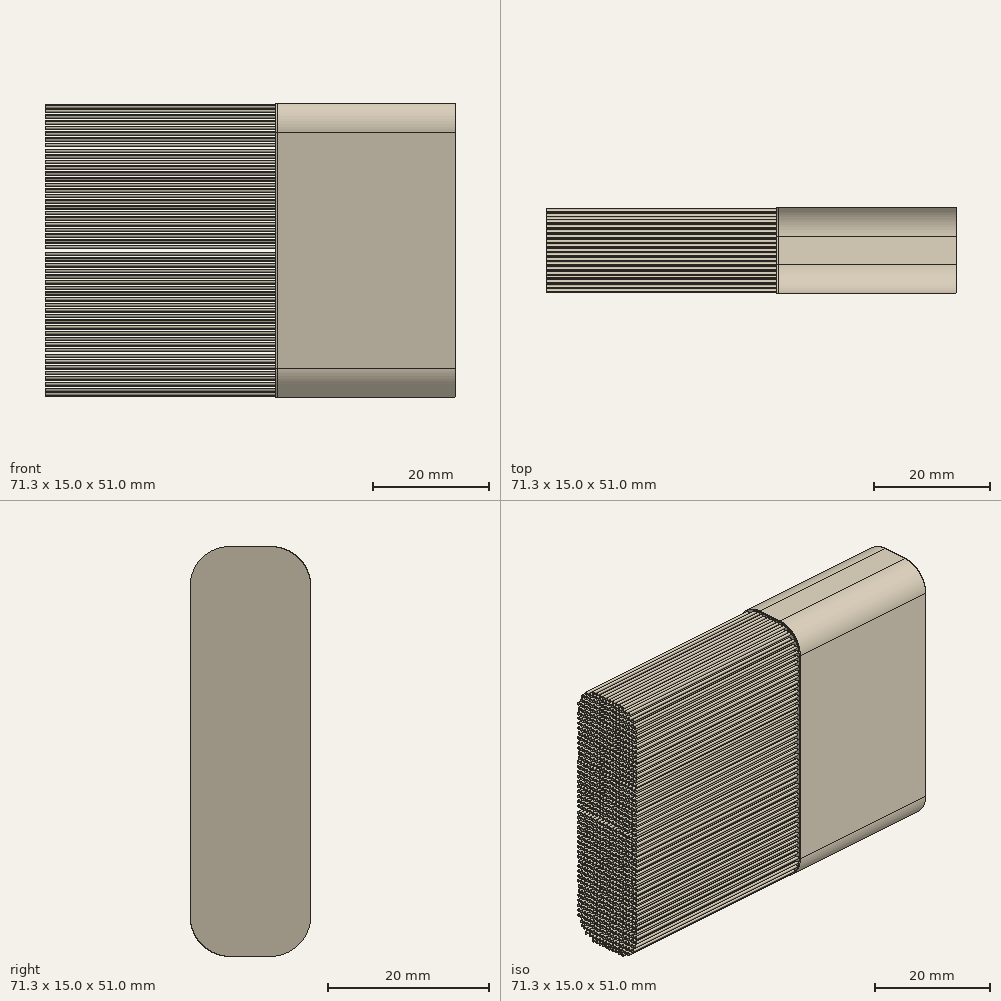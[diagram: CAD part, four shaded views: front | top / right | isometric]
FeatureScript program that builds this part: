
annotation { "Feature Type Name" : "Feature", "Feature Type Description" : "" }
export const myFeature = defineFeature(function(context is Context, id is Id, definition is map)
    precondition{}
    {
        {
            var Q0;
            Q0=qCreatedBy(makeId("Front.planeOp"),FACE);
            var sketch = newSketch(context, id + "F0", { "sketchPlane" : qUnion([Q0])});
            skLineSegment(sketch, "E0.bottom", {"start": v(15.5, -25.5) * mm, "end": v(-15.5, -25.5) * mm});
            skLineSegment(sketch, "E0.top", {"start": v(15.5, 25.5) * mm, "end": v(-15.5, 25.5) * mm});
            skLineSegment(sketch, "E0.left", {"start": v(15.5, -25.5) * mm, "end": v(15.5, 25.5) * mm});
            skLineSegment(sketch, "E0.right", {"start": v(-15.5, -25.5) * mm, "end": v(-15.5, 25.5) * mm});
            skPoint(sketch, "E0.middle", {"position": v(0, 0) * mm});
            skSolve(sketch);
        }
        {
            var Q0;
            Q0=makeQuery(id+"F0.imprint","IMPRINT",FACE,{"disambiguationData":[TD([[makeQuery(id+"F0.imprint","IMPRINT",EDGE,{"derivedFrom":sQuery(id+"F0.wireOp",EDGE,"E0.bottom")}),-1.0]])]});
            extrude(context, id + "F1", {"entities" : qUnion([Q0]), "depth" : 15 * mm});
        }
        {
            var Q0;
            Q0=makeQuery(id+"F1.opExtrude","CAP_EDGE",EDGE,{"disambiguationData":[OSD([sQuery(id+"F0.wireOp",EDGE,"E0.top")])],"isStart":true});
            var Q1;
            Q1=makeQuery(id+"F1.opExtrude","CAP_EDGE",EDGE,{"disambiguationData":[OSD([sQuery(id+"F0.wireOp",EDGE,"E0.bottom")])],"isStart":true});
            var Q2;
            Q2=makeQuery(id+"F1.opExtrude","CAP_EDGE",EDGE,{"disambiguationData":[OSD([sQuery(id+"F0.wireOp",EDGE,"E0.bottom")])],"isStart":false});
            var Q3;
            Q3=makeQuery(id+"F1.opExtrude","CAP_EDGE",EDGE,{"disambiguationData":[OSD([sQuery(id+"F0.wireOp",EDGE,"E0.top")])],"isStart":false});
            fillet(context, id + "F2", {"entities" : qUnion([Q0, Q1, Q2, Q3]), "radius" : 5 * mm, "tangentPropagation" : true, "allowEdgeOverflow" : false});
        }
        {
            var Q0;
            Q0=qCreatedBy(makeId("Right.planeOp"),FACE);
            cPlane(context, id + "F3", {"entities" : qUnion([Q0]), "cplaneType" : CPlaneType.OFFSET, "offset" : 15.8 * mm, "oppositeDirection" : true, "width" : 150 * mm, "height" : 150 * mm});
        }
        {
            var Q0;
            Q0=qCreatedBy(id+"F3.planeOp",FACE);
            var sketch = newSketch(context, id + "F4", { "sketchPlane" : qUnion([Q0])});
            skLineSegment(sketch, "E1.0.0", {"start": v(-10, 25.5) * mm, "end": v(-5, 25.5) * mm});
            skArc(sketch, "E1.0.1", {"start": v(-5, 25.5) * mm, "mid": v(-1.46, 24.04) * mm, "end": v(0, 20.5) * mm});
            skLineSegment(sketch, "E1.0.2", {"start": v(0, 20.5) * mm, "end": v(0, -20.5) * mm});
            skArc(sketch, "E1.0.3", {"start": v(0, -20.5) * mm, "mid": v(-1.46, -24.04) * mm, "end": v(-5, -25.5) * mm});
            skLineSegment(sketch, "E1.0.4", {"start": v(-5, -25.5) * mm, "end": v(-10, -25.5) * mm});
            skArc(sketch, "E1.0.5", {"start": v(-10, -25.5) * mm, "mid": v(-13.54, -24.04) * mm, "end": v(-15, -20.5) * mm});
            skLineSegment(sketch, "E1.0.6", {"start": v(-15, -20.5) * mm, "end": v(-15, 20.5) * mm});
            skArc(sketch, "E1.0.7", {"start": v(-15, 20.5) * mm, "mid": v(-13.54, 24.04) * mm, "end": v(-10, 25.5) * mm});
            skSolve(sketch);
        }
        {
            var Q0;
            Q0=makeQuery(id+"F4.imprint","IMPRINT",FACE,{"disambiguationData":[TD([[makeQuery(id+"F4.imprint","IMPRINT",EDGE,{"derivedFrom":sQuery(id+"F4.wireOp",EDGE,"E1.0.0")}),-1.0]])]});
            extrude(context, id + "F5", {"entities" : qUnion([Q0]), "depth" : 0.3 * mm});
        }
        {
            var Q0;
            Q0=makeQuery(id+"F4.imprint","IMPRINT",FACE,{"disambiguationData":[TD([[makeQuery(id+"F4.imprint","IMPRINT",EDGE,{"derivedFrom":sQuery(id+"F4.wireOp",EDGE,"E1.0.0")}),-1.0]])]});
            var sketch = newSketch(context, id + "F6", { "sketchPlane" : qUnion([Q0])});
            skCircle(sketch, "E2", {"center": v(-8.78, 4.59) * mm, "radius": 0.25 * mm});
            skCircle(sketch, "E3", {"center": v(-9.57, 4.53) * mm, "radius": 0.25 * mm});
            skCircle(sketch, "E4", {"center": v(-10.4, 4.5) * mm, "radius": 0.25 * mm});
            skCircle(sketch, "E5", {"center": v(-11.22, 4.53) * mm, "radius": 0.25 * mm});
            skCircle(sketch, "E6", {"center": v(-8, 4.59) * mm, "radius": 0.25 * mm});
            skCircle(sketch, "E7", {"center": v(-13.64, 4.5) * mm, "radius": 0.25 * mm});
            skCircle(sketch, "E8", {"center": v(-11.98, 4.56) * mm, "radius": 0.25 * mm});
            skCircle(sketch, "E9", {"center": v(-14.45, 4.53) * mm, "radius": 0.25 * mm});
            skCircle(sketch, "E10", {"center": v(-0.37, 4.62) * mm, "radius": 0.25 * mm});
            skCircle(sketch, "E11", {"center": v(-12.74, 4.5) * mm, "radius": 0.25 * mm});
            skCircle(sketch, "E12", {"center": v(-6.43, 4.55) * mm, "radius": 0.25 * mm});
            skCircle(sketch, "E13", {"center": v(-5.64, 4.6) * mm, "radius": 0.25 * mm});
            skCircle(sketch, "E14", {"center": v(-4.8, 4.63) * mm, "radius": 0.25 * mm});
            skCircle(sketch, "E15", {"center": v(-3.99, 4.6) * mm, "radius": 0.25 * mm});
            skCircle(sketch, "E16", {"center": v(-7.22, 4.55) * mm, "radius": 0.25 * mm});
            skCircle(sketch, "E17", {"center": v(-1.78, 4.61) * mm, "radius": 0.25 * mm});
            skCircle(sketch, "E18", {"center": v(-3.23, 4.58) * mm, "radius": 0.25 * mm});
            skCircle(sketch, "E19", {"center": v(-1.03, 4.63) * mm, "radius": 0.25 * mm});
            skCircle(sketch, "E20", {"center": v(-2.47, 4.63) * mm, "radius": 0.25 * mm});
            skCircle(sketch, "E21", {"center": v(-8.86, 3.61) * mm, "radius": 0.25 * mm});
            skCircle(sketch, "E22", {"center": v(-9.64, 3.56) * mm, "radius": 0.25 * mm});
            skCircle(sketch, "E23", {"center": v(-10.48, 3.53) * mm, "radius": 0.25 * mm});
            skCircle(sketch, "E24", {"center": v(-11.3, 3.56) * mm, "radius": 0.25 * mm});
            skCircle(sketch, "E25", {"center": v(-8.07, 3.61) * mm, "radius": 0.25 * mm});
            skCircle(sketch, "E26", {"center": v(-13.71, 3.53) * mm, "radius": 0.25 * mm});
            skCircle(sketch, "E27", {"center": v(-12.06, 3.59) * mm, "radius": 0.25 * mm});
            skCircle(sketch, "E28", {"center": v(-14.52, 3.56) * mm, "radius": 0.25 * mm});
            skCircle(sketch, "E29", {"center": v(-0.44, 3.65) * mm, "radius": 0.25 * mm});
            skCircle(sketch, "E30", {"center": v(-12.82, 3.53) * mm, "radius": 0.25 * mm});
            skCircle(sketch, "E31", {"center": v(-6.5, 3.58) * mm, "radius": 0.25 * mm});
            skCircle(sketch, "E32", {"center": v(-5.72, 3.63) * mm, "radius": 0.25 * mm});
            skCircle(sketch, "E33", {"center": v(-4.88, 3.66) * mm, "radius": 0.25 * mm});
            skCircle(sketch, "E34", {"center": v(-4.06, 3.63) * mm, "radius": 0.25 * mm});
            skCircle(sketch, "E35", {"center": v(-7.3, 3.58) * mm, "radius": 0.25 * mm});
            skCircle(sketch, "E36", {"center": v(-1.86, 3.64) * mm, "radius": 0.25 * mm});
            skCircle(sketch, "E37", {"center": v(-3.3, 3.6) * mm, "radius": 0.25 * mm});
            skCircle(sketch, "E38", {"center": v(-1.1, 3.66) * mm, "radius": 0.25 * mm});
            skCircle(sketch, "E39", {"center": v(-2.54, 3.66) * mm, "radius": 0.25 * mm});
            skCircle(sketch, "E40", {"center": v(-8.86, 2.59) * mm, "radius": 0.25 * mm});
            skCircle(sketch, "E41", {"center": v(-9.64, 2.54) * mm, "radius": 0.25 * mm});
            skCircle(sketch, "E42", {"center": v(-10.48, 2.51) * mm, "radius": 0.25 * mm});
            skCircle(sketch, "E43", {"center": v(-11.3, 2.54) * mm, "radius": 0.25 * mm});
            skCircle(sketch, "E44", {"center": v(-8.07, 2.59) * mm, "radius": 0.25 * mm});
            skCircle(sketch, "E45", {"center": v(-13.71, 2.51) * mm, "radius": 0.25 * mm});
            skCircle(sketch, "E46", {"center": v(-12.06, 2.56) * mm, "radius": 0.25 * mm});
            skCircle(sketch, "E47", {"center": v(-14.52, 2.54) * mm, "radius": 0.25 * mm});
            skCircle(sketch, "E48", {"center": v(-0.44, 2.63) * mm, "radius": 0.25 * mm});
            skCircle(sketch, "E49", {"center": v(-12.82, 2.51) * mm, "radius": 0.25 * mm});
            skCircle(sketch, "E50", {"center": v(-6.5, 2.56) * mm, "radius": 0.25 * mm});
            skCircle(sketch, "E51", {"center": v(-5.72, 2.6) * mm, "radius": 0.25 * mm});
            skCircle(sketch, "E52", {"center": v(-4.88, 2.64) * mm, "radius": 0.25 * mm});
            skCircle(sketch, "E53", {"center": v(-4.06, 2.6) * mm, "radius": 0.25 * mm});
            skCircle(sketch, "E54", {"center": v(-7.3, 2.56) * mm, "radius": 0.25 * mm});
            skCircle(sketch, "E55", {"center": v(-1.86, 2.62) * mm, "radius": 0.25 * mm});
            skCircle(sketch, "E56", {"center": v(-3.3, 2.58) * mm, "radius": 0.25 * mm});
            skCircle(sketch, "E57", {"center": v(-1.1, 2.64) * mm, "radius": 0.25 * mm});
            skCircle(sketch, "E58", {"center": v(-2.54, 2.64) * mm, "radius": 0.25 * mm});
            skCircle(sketch, "E59", {"center": v(-8.86, 1.62) * mm, "radius": 0.25 * mm});
            skCircle(sketch, "E60", {"center": v(-9.64, 1.56) * mm, "radius": 0.25 * mm});
            skCircle(sketch, "E61", {"center": v(-10.48, 1.54) * mm, "radius": 0.25 * mm});
            skCircle(sketch, "E62", {"center": v(-11.3, 1.56) * mm, "radius": 0.25 * mm});
            skCircle(sketch, "E63", {"center": v(-8.07, 1.62) * mm, "radius": 0.25 * mm});
            skCircle(sketch, "E64", {"center": v(-13.71, 1.54) * mm, "radius": 0.25 * mm});
            skCircle(sketch, "E65", {"center": v(-12.06, 1.6) * mm, "radius": 0.25 * mm});
            skCircle(sketch, "E66", {"center": v(-14.52, 1.56) * mm, "radius": 0.25 * mm});
            skCircle(sketch, "E67", {"center": v(-0.44, 1.65) * mm, "radius": 0.25 * mm});
            skCircle(sketch, "E68", {"center": v(-12.82, 1.54) * mm, "radius": 0.25 * mm});
            skCircle(sketch, "E69", {"center": v(-6.5, 1.58) * mm, "radius": 0.25 * mm});
            skCircle(sketch, "E70", {"center": v(-5.72, 1.64) * mm, "radius": 0.25 * mm});
            skCircle(sketch, "E71", {"center": v(-4.88, 1.66) * mm, "radius": 0.25 * mm});
            skCircle(sketch, "E72", {"center": v(-4.06, 1.64) * mm, "radius": 0.25 * mm});
            skCircle(sketch, "E73", {"center": v(-7.3, 1.58) * mm, "radius": 0.25 * mm});
            skCircle(sketch, "E74", {"center": v(-1.86, 1.64) * mm, "radius": 0.25 * mm});
            skCircle(sketch, "E75", {"center": v(-3.3, 1.61) * mm, "radius": 0.25 * mm});
            skCircle(sketch, "E76", {"center": v(-1.1, 1.66) * mm, "radius": 0.25 * mm});
            skCircle(sketch, "E77", {"center": v(-2.54, 1.66) * mm, "radius": 0.25 * mm});
            skCircle(sketch, "E78", {"center": v(-8.9, 0.62) * mm, "radius": 0.25 * mm});
            skCircle(sketch, "E79", {"center": v(-9.69, 0.57) * mm, "radius": 0.25 * mm});
            skCircle(sketch, "E80", {"center": v(-10.52, 0.54) * mm, "radius": 0.25 * mm});
            skCircle(sketch, "E81", {"center": v(-11.34, 0.57) * mm, "radius": 0.25 * mm});
            skCircle(sketch, "E82", {"center": v(-8.11, 0.62) * mm, "radius": 0.25 * mm});
            skCircle(sketch, "E83", {"center": v(-13.75, 0.54) * mm, "radius": 0.25 * mm});
            skCircle(sketch, "E84", {"center": v(-12.1, 0.6) * mm, "radius": 0.25 * mm});
            skCircle(sketch, "E85", {"center": v(-14.57, 0.57) * mm, "radius": 0.25 * mm});
            skCircle(sketch, "E86", {"center": v(-0.49, 0.66) * mm, "radius": 0.25 * mm});
            skCircle(sketch, "E87", {"center": v(-12.86, 0.54) * mm, "radius": 0.25 * mm});
            skCircle(sketch, "E88", {"center": v(-6.55, 0.6) * mm, "radius": 0.25 * mm});
            skCircle(sketch, "E89", {"center": v(-5.76, 0.64) * mm, "radius": 0.25 * mm});
            skCircle(sketch, "E90", {"center": v(-4.92, 0.67) * mm, "radius": 0.25 * mm});
            skCircle(sketch, "E91", {"center": v(-4.1, 0.64) * mm, "radius": 0.25 * mm});
            skCircle(sketch, "E92", {"center": v(-7.33, 0.6) * mm, "radius": 0.25 * mm});
            skCircle(sketch, "E93", {"center": v(-1.9, 0.65) * mm, "radius": 0.25 * mm});
            skCircle(sketch, "E94", {"center": v(-3.34, 0.62) * mm, "radius": 0.25 * mm});
            skCircle(sketch, "E95", {"center": v(-1.14, 0.67) * mm, "radius": 0.25 * mm});
            skCircle(sketch, "E96", {"center": v(-2.58, 0.67) * mm, "radius": 0.25 * mm});
            skCircle(sketch, "E97", {"center": v(-8.78, 9.52) * mm, "radius": 0.25 * mm});
            skCircle(sketch, "E98", {"center": v(-9.57, 9.47) * mm, "radius": 0.25 * mm});
            skCircle(sketch, "E99", {"center": v(-10.4, 9.44) * mm, "radius": 0.25 * mm});
            skCircle(sketch, "E100", {"center": v(-11.22, 9.47) * mm, "radius": 0.25 * mm});
            skCircle(sketch, "E101", {"center": v(-8, 9.52) * mm, "radius": 0.25 * mm});
            skCircle(sketch, "E102", {"center": v(-13.64, 9.44) * mm, "radius": 0.25 * mm});
            skCircle(sketch, "E103", {"center": v(-11.98, 9.5) * mm, "radius": 0.25 * mm});
            skCircle(sketch, "E104", {"center": v(-14.45, 9.47) * mm, "radius": 0.25 * mm});
            skCircle(sketch, "E105", {"center": v(-0.37, 9.56) * mm, "radius": 0.25 * mm});
            skCircle(sketch, "E106", {"center": v(-12.74, 9.44) * mm, "radius": 0.25 * mm});
            skCircle(sketch, "E107", {"center": v(-6.43, 9.5) * mm, "radius": 0.25 * mm});
            skCircle(sketch, "E108", {"center": v(-5.64, 9.54) * mm, "radius": 0.25 * mm});
            skCircle(sketch, "E109", {"center": v(-4.8, 9.57) * mm, "radius": 0.25 * mm});
            skCircle(sketch, "E110", {"center": v(-3.99, 9.54) * mm, "radius": 0.25 * mm});
            skCircle(sketch, "E111", {"center": v(-7.22, 9.5) * mm, "radius": 0.25 * mm});
            skCircle(sketch, "E112", {"center": v(-1.78, 9.55) * mm, "radius": 0.25 * mm});
            skCircle(sketch, "E113", {"center": v(-3.23, 9.52) * mm, "radius": 0.25 * mm});
            skCircle(sketch, "E114", {"center": v(-1.03, 9.57) * mm, "radius": 0.25 * mm});
            skCircle(sketch, "E115", {"center": v(-2.47, 9.57) * mm, "radius": 0.25 * mm});
            skCircle(sketch, "E116", {"center": v(-8.86, 8.55) * mm, "radius": 0.25 * mm});
            skCircle(sketch, "E117", {"center": v(-9.64, 8.5) * mm, "radius": 0.25 * mm});
            skCircle(sketch, "E118", {"center": v(-10.48, 8.47) * mm, "radius": 0.25 * mm});
            skCircle(sketch, "E119", {"center": v(-11.3, 8.5) * mm, "radius": 0.25 * mm});
            skCircle(sketch, "E120", {"center": v(-8.07, 8.55) * mm, "radius": 0.25 * mm});
            skCircle(sketch, "E121", {"center": v(-13.71, 8.47) * mm, "radius": 0.25 * mm});
            skCircle(sketch, "E122", {"center": v(-12.06, 8.52) * mm, "radius": 0.25 * mm});
            skCircle(sketch, "E123", {"center": v(-14.52, 8.5) * mm, "radius": 0.25 * mm});
            skCircle(sketch, "E124", {"center": v(-0.44, 8.59) * mm, "radius": 0.25 * mm});
            skCircle(sketch, "E125", {"center": v(-12.82, 8.47) * mm, "radius": 0.25 * mm});
            skCircle(sketch, "E126", {"center": v(-6.5, 8.52) * mm, "radius": 0.25 * mm});
            skCircle(sketch, "E127", {"center": v(-5.72, 8.57) * mm, "radius": 0.25 * mm});
            skCircle(sketch, "E128", {"center": v(-4.88, 8.6) * mm, "radius": 0.25 * mm});
            skCircle(sketch, "E129", {"center": v(-4.06, 8.57) * mm, "radius": 0.25 * mm});
            skCircle(sketch, "E130", {"center": v(-7.3, 8.52) * mm, "radius": 0.25 * mm});
            skCircle(sketch, "E131", {"center": v(-1.86, 8.58) * mm, "radius": 0.25 * mm});
            skCircle(sketch, "E132", {"center": v(-3.3, 8.54) * mm, "radius": 0.25 * mm});
            skCircle(sketch, "E133", {"center": v(-1.1, 8.6) * mm, "radius": 0.25 * mm});
            skCircle(sketch, "E134", {"center": v(-2.54, 8.6) * mm, "radius": 0.25 * mm});
            skCircle(sketch, "E135", {"center": v(-8.86, 7.53) * mm, "radius": 0.25 * mm});
            skCircle(sketch, "E136", {"center": v(-9.64, 7.47) * mm, "radius": 0.25 * mm});
            skCircle(sketch, "E137", {"center": v(-10.48, 7.45) * mm, "radius": 0.25 * mm});
            skCircle(sketch, "E138", {"center": v(-11.3, 7.47) * mm, "radius": 0.25 * mm});
            skCircle(sketch, "E139", {"center": v(-8.07, 7.53) * mm, "radius": 0.25 * mm});
            skCircle(sketch, "E140", {"center": v(-13.71, 7.45) * mm, "radius": 0.25 * mm});
            skCircle(sketch, "E141", {"center": v(-12.06, 7.5) * mm, "radius": 0.25 * mm});
            skCircle(sketch, "E142", {"center": v(-14.52, 7.47) * mm, "radius": 0.25 * mm});
            skCircle(sketch, "E143", {"center": v(-0.44, 7.56) * mm, "radius": 0.25 * mm});
            skCircle(sketch, "E144", {"center": v(-12.82, 7.45) * mm, "radius": 0.25 * mm});
            skCircle(sketch, "E145", {"center": v(-6.5, 7.5) * mm, "radius": 0.25 * mm});
            skCircle(sketch, "E146", {"center": v(-5.72, 7.55) * mm, "radius": 0.25 * mm});
            skCircle(sketch, "E147", {"center": v(-4.88, 7.57) * mm, "radius": 0.25 * mm});
            skCircle(sketch, "E148", {"center": v(-4.06, 7.55) * mm, "radius": 0.25 * mm});
            skCircle(sketch, "E149", {"center": v(-7.3, 7.5) * mm, "radius": 0.25 * mm});
            skCircle(sketch, "E150", {"center": v(-1.86, 7.55) * mm, "radius": 0.25 * mm});
            skCircle(sketch, "E151", {"center": v(-3.3, 7.52) * mm, "radius": 0.25 * mm});
            skCircle(sketch, "E152", {"center": v(-1.1, 7.57) * mm, "radius": 0.25 * mm});
            skCircle(sketch, "E153", {"center": v(-2.54, 7.57) * mm, "radius": 0.25 * mm});
            skCircle(sketch, "E154", {"center": v(-8.86, 6.55) * mm, "radius": 0.25 * mm});
            skCircle(sketch, "E155", {"center": v(-9.64, 6.5) * mm, "radius": 0.25 * mm});
            skCircle(sketch, "E156", {"center": v(-10.48, 6.47) * mm, "radius": 0.25 * mm});
            skCircle(sketch, "E157", {"center": v(-11.3, 6.5) * mm, "radius": 0.25 * mm});
            skCircle(sketch, "E158", {"center": v(-8.07, 6.55) * mm, "radius": 0.25 * mm});
            skCircle(sketch, "E159", {"center": v(-13.71, 6.47) * mm, "radius": 0.25 * mm});
            skCircle(sketch, "E160", {"center": v(-12.06, 6.53) * mm, "radius": 0.25 * mm});
            skCircle(sketch, "E161", {"center": v(-14.52, 6.5) * mm, "radius": 0.25 * mm});
            skCircle(sketch, "E162", {"center": v(-0.44, 6.6) * mm, "radius": 0.25 * mm});
            skCircle(sketch, "E163", {"center": v(-12.82, 6.47) * mm, "radius": 0.25 * mm});
            skCircle(sketch, "E164", {"center": v(-6.5, 6.52) * mm, "radius": 0.25 * mm});
            skCircle(sketch, "E165", {"center": v(-5.72, 6.57) * mm, "radius": 0.25 * mm});
            skCircle(sketch, "E166", {"center": v(-4.88, 6.6) * mm, "radius": 0.25 * mm});
            skCircle(sketch, "E167", {"center": v(-4.06, 6.57) * mm, "radius": 0.25 * mm});
            skCircle(sketch, "E168", {"center": v(-7.3, 6.52) * mm, "radius": 0.25 * mm});
            skCircle(sketch, "E169", {"center": v(-1.86, 6.58) * mm, "radius": 0.25 * mm});
            skCircle(sketch, "E170", {"center": v(-3.3, 6.55) * mm, "radius": 0.25 * mm});
            skCircle(sketch, "E171", {"center": v(-1.1, 6.6) * mm, "radius": 0.25 * mm});
            skCircle(sketch, "E172", {"center": v(-2.54, 6.6) * mm, "radius": 0.25 * mm});
            skCircle(sketch, "E173", {"center": v(-8.9, 5.56) * mm, "radius": 0.25 * mm});
            skCircle(sketch, "E174", {"center": v(-9.69, 5.5) * mm, "radius": 0.25 * mm});
            skCircle(sketch, "E175", {"center": v(-10.52, 5.48) * mm, "radius": 0.25 * mm});
            skCircle(sketch, "E176", {"center": v(-11.34, 5.5) * mm, "radius": 0.25 * mm});
            skCircle(sketch, "E177", {"center": v(-8.11, 5.56) * mm, "radius": 0.25 * mm});
            skCircle(sketch, "E178", {"center": v(-13.75, 5.48) * mm, "radius": 0.25 * mm});
            skCircle(sketch, "E179", {"center": v(-12.1, 5.53) * mm, "radius": 0.25 * mm});
            skCircle(sketch, "E180", {"center": v(-14.57, 5.5) * mm, "radius": 0.25 * mm});
            skCircle(sketch, "E181", {"center": v(-0.49, 5.6) * mm, "radius": 0.25 * mm});
            skCircle(sketch, "E182", {"center": v(-12.86, 5.48) * mm, "radius": 0.25 * mm});
            skCircle(sketch, "E183", {"center": v(-6.55, 5.53) * mm, "radius": 0.25 * mm});
            skCircle(sketch, "E184", {"center": v(-5.76, 5.58) * mm, "radius": 0.25 * mm});
            skCircle(sketch, "E185", {"center": v(-4.92, 5.6) * mm, "radius": 0.25 * mm});
            skCircle(sketch, "E186", {"center": v(-4.1, 5.58) * mm, "radius": 0.25 * mm});
            skCircle(sketch, "E187", {"center": v(-7.33, 5.53) * mm, "radius": 0.25 * mm});
            skCircle(sketch, "E188", {"center": v(-1.9, 5.59) * mm, "radius": 0.25 * mm});
            skCircle(sketch, "E189", {"center": v(-3.34, 5.55) * mm, "radius": 0.25 * mm});
            skCircle(sketch, "E190", {"center": v(-1.14, 5.6) * mm, "radius": 0.25 * mm});
            skCircle(sketch, "E191", {"center": v(-2.58, 5.6) * mm, "radius": 0.25 * mm});
            skCircle(sketch, "E192", {"center": v(-8.86, 14.4) * mm, "radius": 0.25 * mm});
            skCircle(sketch, "E193", {"center": v(-9.64, 14.35) * mm, "radius": 0.25 * mm});
            skCircle(sketch, "E194", {"center": v(-10.48, 14.32) * mm, "radius": 0.25 * mm});
            skCircle(sketch, "E195", {"center": v(-11.3, 14.35) * mm, "radius": 0.25 * mm});
            skCircle(sketch, "E196", {"center": v(-8.07, 14.4) * mm, "radius": 0.25 * mm});
            skCircle(sketch, "E197", {"center": v(-13.71, 14.32) * mm, "radius": 0.25 * mm});
            skCircle(sketch, "E198", {"center": v(-12.06, 14.38) * mm, "radius": 0.25 * mm});
            skCircle(sketch, "E199", {"center": v(-14.52, 14.35) * mm, "radius": 0.25 * mm});
            skCircle(sketch, "E200", {"center": v(-0.44, 14.44) * mm, "radius": 0.25 * mm});
            skCircle(sketch, "E201", {"center": v(-12.82, 14.32) * mm, "radius": 0.25 * mm});
            skCircle(sketch, "E202", {"center": v(-6.5, 14.37) * mm, "radius": 0.25 * mm});
            skCircle(sketch, "E203", {"center": v(-5.72, 14.42) * mm, "radius": 0.25 * mm});
            skCircle(sketch, "E204", {"center": v(-4.88, 14.45) * mm, "radius": 0.25 * mm});
            skCircle(sketch, "E205", {"center": v(-4.06, 14.42) * mm, "radius": 0.25 * mm});
            skCircle(sketch, "E206", {"center": v(-7.3, 14.37) * mm, "radius": 0.25 * mm});
            skCircle(sketch, "E207", {"center": v(-1.86, 14.43) * mm, "radius": 0.25 * mm});
            skCircle(sketch, "E208", {"center": v(-3.3, 14.4) * mm, "radius": 0.25 * mm});
            skCircle(sketch, "E209", {"center": v(-1.1, 14.45) * mm, "radius": 0.25 * mm});
            skCircle(sketch, "E210", {"center": v(-2.54, 14.45) * mm, "radius": 0.25 * mm});
            skCircle(sketch, "E211", {"center": v(-8.93, 13.43) * mm, "radius": 0.25 * mm});
            skCircle(sketch, "E212", {"center": v(-9.72, 13.38) * mm, "radius": 0.25 * mm});
            skCircle(sketch, "E213", {"center": v(-10.56, 13.35) * mm, "radius": 0.25 * mm});
            skCircle(sketch, "E214", {"center": v(-11.37, 13.38) * mm, "radius": 0.25 * mm});
            skCircle(sketch, "E215", {"center": v(-8.14, 13.43) * mm, "radius": 0.25 * mm});
            skCircle(sketch, "E216", {"center": v(-13.79, 13.35) * mm, "radius": 0.25 * mm});
            skCircle(sketch, "E217", {"center": v(-12.13, 13.4) * mm, "radius": 0.25 * mm});
            skCircle(sketch, "E218", {"center": v(-14.6, 13.38) * mm, "radius": 0.25 * mm});
            skCircle(sketch, "E219", {"center": v(-0.52, 13.46) * mm, "radius": 0.25 * mm});
            skCircle(sketch, "E220", {"center": v(-12.9, 13.35) * mm, "radius": 0.25 * mm});
            skCircle(sketch, "E221", {"center": v(-6.58, 13.4) * mm, "radius": 0.25 * mm});
            skCircle(sketch, "E222", {"center": v(-5.8, 13.45) * mm, "radius": 0.25 * mm});
            skCircle(sketch, "E223", {"center": v(-4.95, 13.47) * mm, "radius": 0.25 * mm});
            skCircle(sketch, "E224", {"center": v(-4.14, 13.45) * mm, "radius": 0.25 * mm});
            skCircle(sketch, "E225", {"center": v(-7.37, 13.4) * mm, "radius": 0.25 * mm});
            skCircle(sketch, "E226", {"center": v(-1.93, 13.46) * mm, "radius": 0.25 * mm});
            skCircle(sketch, "E227", {"center": v(-3.38, 13.42) * mm, "radius": 0.25 * mm});
            skCircle(sketch, "E228", {"center": v(-1.18, 13.47) * mm, "radius": 0.25 * mm});
            skCircle(sketch, "E229", {"center": v(-2.62, 13.47) * mm, "radius": 0.25 * mm});
            skCircle(sketch, "E230", {"center": v(-8.93, 12.4) * mm, "radius": 0.25 * mm});
            skCircle(sketch, "E231", {"center": v(-9.72, 12.35) * mm, "radius": 0.25 * mm});
            skCircle(sketch, "E232", {"center": v(-10.56, 12.33) * mm, "radius": 0.25 * mm});
            skCircle(sketch, "E233", {"center": v(-11.37, 12.35) * mm, "radius": 0.25 * mm});
            skCircle(sketch, "E234", {"center": v(-8.14, 12.4) * mm, "radius": 0.25 * mm});
            skCircle(sketch, "E235", {"center": v(-13.79, 12.33) * mm, "radius": 0.25 * mm});
            skCircle(sketch, "E236", {"center": v(-12.13, 12.38) * mm, "radius": 0.25 * mm});
            skCircle(sketch, "E237", {"center": v(-14.6, 12.35) * mm, "radius": 0.25 * mm});
            skCircle(sketch, "E238", {"center": v(-0.52, 12.44) * mm, "radius": 0.25 * mm});
            skCircle(sketch, "E239", {"center": v(-12.9, 12.33) * mm, "radius": 0.25 * mm});
            skCircle(sketch, "E240", {"center": v(-6.58, 12.37) * mm, "radius": 0.25 * mm});
            skCircle(sketch, "E241", {"center": v(-5.8, 12.43) * mm, "radius": 0.25 * mm});
            skCircle(sketch, "E242", {"center": v(-4.95, 12.45) * mm, "radius": 0.25 * mm});
            skCircle(sketch, "E243", {"center": v(-4.14, 12.43) * mm, "radius": 0.25 * mm});
            skCircle(sketch, "E244", {"center": v(-7.37, 12.37) * mm, "radius": 0.25 * mm});
            skCircle(sketch, "E245", {"center": v(-1.93, 12.43) * mm, "radius": 0.25 * mm});
            skCircle(sketch, "E246", {"center": v(-3.38, 12.4) * mm, "radius": 0.25 * mm});
            skCircle(sketch, "E247", {"center": v(-1.18, 12.45) * mm, "radius": 0.25 * mm});
            skCircle(sketch, "E248", {"center": v(-2.62, 12.45) * mm, "radius": 0.25 * mm});
            skCircle(sketch, "E249", {"center": v(-8.93, 11.43) * mm, "radius": 0.25 * mm});
            skCircle(sketch, "E250", {"center": v(-9.72, 11.38) * mm, "radius": 0.25 * mm});
            skCircle(sketch, "E251", {"center": v(-10.56, 11.35) * mm, "radius": 0.25 * mm});
            skCircle(sketch, "E252", {"center": v(-11.37, 11.38) * mm, "radius": 0.25 * mm});
            skCircle(sketch, "E253", {"center": v(-8.14, 11.43) * mm, "radius": 0.25 * mm});
            skCircle(sketch, "E254", {"center": v(-13.79, 11.35) * mm, "radius": 0.25 * mm});
            skCircle(sketch, "E255", {"center": v(-12.13, 11.4) * mm, "radius": 0.25 * mm});
            skCircle(sketch, "E256", {"center": v(-14.6, 11.38) * mm, "radius": 0.25 * mm});
            skCircle(sketch, "E257", {"center": v(-0.52, 11.47) * mm, "radius": 0.25 * mm});
            skCircle(sketch, "E258", {"center": v(-12.9, 11.35) * mm, "radius": 0.25 * mm});
            skCircle(sketch, "E259", {"center": v(-6.58, 11.4) * mm, "radius": 0.25 * mm});
            skCircle(sketch, "E260", {"center": v(-5.8, 11.45) * mm, "radius": 0.25 * mm});
            skCircle(sketch, "E261", {"center": v(-4.95, 11.48) * mm, "radius": 0.25 * mm});
            skCircle(sketch, "E262", {"center": v(-4.14, 11.45) * mm, "radius": 0.25 * mm});
            skCircle(sketch, "E263", {"center": v(-7.37, 11.4) * mm, "radius": 0.25 * mm});
            skCircle(sketch, "E264", {"center": v(-1.93, 11.46) * mm, "radius": 0.25 * mm});
            skCircle(sketch, "E265", {"center": v(-3.38, 11.43) * mm, "radius": 0.25 * mm});
            skCircle(sketch, "E266", {"center": v(-1.18, 11.48) * mm, "radius": 0.25 * mm});
            skCircle(sketch, "E267", {"center": v(-2.62, 11.48) * mm, "radius": 0.25 * mm});
            skCircle(sketch, "E268", {"center": v(-8.97, 10.44) * mm, "radius": 0.25 * mm});
            skCircle(sketch, "E269", {"center": v(-9.76, 10.39) * mm, "radius": 0.25 * mm});
            skCircle(sketch, "E270", {"center": v(-10.6, 10.36) * mm, "radius": 0.25 * mm});
            skCircle(sketch, "E271", {"center": v(-11.41, 10.39) * mm, "radius": 0.25 * mm});
            skCircle(sketch, "E272", {"center": v(-8.19, 10.44) * mm, "radius": 0.25 * mm});
            skCircle(sketch, "E273", {"center": v(-13.83, 10.36) * mm, "radius": 0.25 * mm});
            skCircle(sketch, "E274", {"center": v(-12.17, 10.41) * mm, "radius": 0.25 * mm});
            skCircle(sketch, "E275", {"center": v(-14.64, 10.39) * mm, "radius": 0.25 * mm});
            skCircle(sketch, "E276", {"center": v(-0.56, 10.48) * mm, "radius": 0.25 * mm});
            skCircle(sketch, "E277", {"center": v(-12.94, 10.36) * mm, "radius": 0.25 * mm});
            skCircle(sketch, "E278", {"center": v(-6.62, 10.4) * mm, "radius": 0.25 * mm});
            skCircle(sketch, "E279", {"center": v(-5.83, 10.46) * mm, "radius": 0.25 * mm});
            skCircle(sketch, "E280", {"center": v(-5, 10.49) * mm, "radius": 0.25 * mm});
            skCircle(sketch, "E281", {"center": v(-4.18, 10.46) * mm, "radius": 0.25 * mm});
            skCircle(sketch, "E282", {"center": v(-7.4, 10.4) * mm, "radius": 0.25 * mm});
            skCircle(sketch, "E283", {"center": v(-1.98, 10.47) * mm, "radius": 0.25 * mm});
            skCircle(sketch, "E284", {"center": v(-3.42, 10.43) * mm, "radius": 0.25 * mm});
            skCircle(sketch, "E285", {"center": v(-1.22, 10.49) * mm, "radius": 0.25 * mm});
            skCircle(sketch, "E286", {"center": v(-2.66, 10.49) * mm, "radius": 0.25 * mm});
            skCircle(sketch, "E287", {"center": v(-8.86, 19.34) * mm, "radius": 0.25 * mm});
            skCircle(sketch, "E288", {"center": v(-9.64, 19.29) * mm, "radius": 0.25 * mm});
            skCircle(sketch, "E289", {"center": v(-10.48, 19.26) * mm, "radius": 0.25 * mm});
            skCircle(sketch, "E290", {"center": v(-11.3, 19.29) * mm, "radius": 0.25 * mm});
            skCircle(sketch, "E291", {"center": v(-8.07, 19.34) * mm, "radius": 0.25 * mm});
            skCircle(sketch, "E292", {"center": v(-13.71, 19.26) * mm, "radius": 0.25 * mm});
            skCircle(sketch, "E293", {"center": v(-12.06, 19.31) * mm, "radius": 0.25 * mm});
            skCircle(sketch, "E294", {"center": v(-14.52, 19.29) * mm, "radius": 0.25 * mm});
            skCircle(sketch, "E295", {"center": v(-0.44, 19.38) * mm, "radius": 0.25 * mm});
            skCircle(sketch, "E296", {"center": v(-12.82, 19.26) * mm, "radius": 0.25 * mm});
            skCircle(sketch, "E297", {"center": v(-6.5, 19.3) * mm, "radius": 0.25 * mm});
            skCircle(sketch, "E298", {"center": v(-5.72, 19.36) * mm, "radius": 0.25 * mm});
            skCircle(sketch, "E299", {"center": v(-4.88, 19.39) * mm, "radius": 0.25 * mm});
            skCircle(sketch, "E300", {"center": v(-4.06, 19.36) * mm, "radius": 0.25 * mm});
            skCircle(sketch, "E301", {"center": v(-7.3, 19.3) * mm, "radius": 0.25 * mm});
            skCircle(sketch, "E302", {"center": v(-1.86, 19.37) * mm, "radius": 0.25 * mm});
            skCircle(sketch, "E303", {"center": v(-3.3, 19.33) * mm, "radius": 0.25 * mm});
            skCircle(sketch, "E304", {"center": v(-1.1, 19.39) * mm, "radius": 0.25 * mm});
            skCircle(sketch, "E305", {"center": v(-2.54, 19.39) * mm, "radius": 0.25 * mm});
            skCircle(sketch, "E306", {"center": v(-8.93, 18.36) * mm, "radius": 0.25 * mm});
            skCircle(sketch, "E307", {"center": v(-9.72, 18.31) * mm, "radius": 0.25 * mm});
            skCircle(sketch, "E308", {"center": v(-10.56, 18.29) * mm, "radius": 0.25 * mm});
            skCircle(sketch, "E309", {"center": v(-11.37, 18.31) * mm, "radius": 0.25 * mm});
            skCircle(sketch, "E310", {"center": v(-8.14, 18.36) * mm, "radius": 0.25 * mm});
            skCircle(sketch, "E311", {"center": v(-13.79, 18.29) * mm, "radius": 0.25 * mm});
            skCircle(sketch, "E312", {"center": v(-12.13, 18.34) * mm, "radius": 0.25 * mm});
            skCircle(sketch, "E313", {"center": v(-14.6, 18.31) * mm, "radius": 0.25 * mm});
            skCircle(sketch, "E314", {"center": v(-0.52, 18.4) * mm, "radius": 0.25 * mm});
            skCircle(sketch, "E315", {"center": v(-12.9, 18.29) * mm, "radius": 0.25 * mm});
            skCircle(sketch, "E316", {"center": v(-6.58, 18.33) * mm, "radius": 0.25 * mm});
            skCircle(sketch, "E317", {"center": v(-5.8, 18.38) * mm, "radius": 0.25 * mm});
            skCircle(sketch, "E318", {"center": v(-4.95, 18.41) * mm, "radius": 0.25 * mm});
            skCircle(sketch, "E319", {"center": v(-4.14, 18.38) * mm, "radius": 0.25 * mm});
            skCircle(sketch, "E320", {"center": v(-7.37, 18.33) * mm, "radius": 0.25 * mm});
            skCircle(sketch, "E321", {"center": v(-1.93, 18.4) * mm, "radius": 0.25 * mm});
            skCircle(sketch, "E322", {"center": v(-3.38, 18.36) * mm, "radius": 0.25 * mm});
            skCircle(sketch, "E323", {"center": v(-1.18, 18.41) * mm, "radius": 0.25 * mm});
            skCircle(sketch, "E324", {"center": v(-2.62, 18.41) * mm, "radius": 0.25 * mm});
            skCircle(sketch, "E325", {"center": v(-8.93, 17.34) * mm, "radius": 0.25 * mm});
            skCircle(sketch, "E326", {"center": v(-9.72, 17.29) * mm, "radius": 0.25 * mm});
            skCircle(sketch, "E327", {"center": v(-10.56, 17.26) * mm, "radius": 0.25 * mm});
            skCircle(sketch, "E328", {"center": v(-11.37, 17.29) * mm, "radius": 0.25 * mm});
            skCircle(sketch, "E329", {"center": v(-8.14, 17.34) * mm, "radius": 0.25 * mm});
            skCircle(sketch, "E330", {"center": v(-13.79, 17.26) * mm, "radius": 0.25 * mm});
            skCircle(sketch, "E331", {"center": v(-12.13, 17.32) * mm, "radius": 0.25 * mm});
            skCircle(sketch, "E332", {"center": v(-14.6, 17.29) * mm, "radius": 0.25 * mm});
            skCircle(sketch, "E333", {"center": v(-0.52, 17.38) * mm, "radius": 0.25 * mm});
            skCircle(sketch, "E334", {"center": v(-12.9, 17.26) * mm, "radius": 0.25 * mm});
            skCircle(sketch, "E335", {"center": v(-6.58, 17.31) * mm, "radius": 0.25 * mm});
            skCircle(sketch, "E336", {"center": v(-5.8, 17.36) * mm, "radius": 0.25 * mm});
            skCircle(sketch, "E337", {"center": v(-4.95, 17.39) * mm, "radius": 0.25 * mm});
            skCircle(sketch, "E338", {"center": v(-4.14, 17.36) * mm, "radius": 0.25 * mm});
            skCircle(sketch, "E339", {"center": v(-7.37, 17.31) * mm, "radius": 0.25 * mm});
            skCircle(sketch, "E340", {"center": v(-1.93, 17.37) * mm, "radius": 0.25 * mm});
            skCircle(sketch, "E341", {"center": v(-3.38, 17.34) * mm, "radius": 0.25 * mm});
            skCircle(sketch, "E342", {"center": v(-1.18, 17.39) * mm, "radius": 0.25 * mm});
            skCircle(sketch, "E343", {"center": v(-2.62, 17.39) * mm, "radius": 0.25 * mm});
            skCircle(sketch, "E344", {"center": v(-8.93, 16.37) * mm, "radius": 0.25 * mm});
            skCircle(sketch, "E345", {"center": v(-9.72, 16.32) * mm, "radius": 0.25 * mm});
            skCircle(sketch, "E346", {"center": v(-10.56, 16.3) * mm, "radius": 0.25 * mm});
            skCircle(sketch, "E347", {"center": v(-11.37, 16.32) * mm, "radius": 0.25 * mm});
            skCircle(sketch, "E348", {"center": v(-8.14, 16.37) * mm, "radius": 0.25 * mm});
            skCircle(sketch, "E349", {"center": v(-13.79, 16.3) * mm, "radius": 0.25 * mm});
            skCircle(sketch, "E350", {"center": v(-12.13, 16.34) * mm, "radius": 0.25 * mm});
            skCircle(sketch, "E351", {"center": v(-14.6, 16.32) * mm, "radius": 0.25 * mm});
            skCircle(sketch, "E352", {"center": v(-0.52, 16.4) * mm, "radius": 0.25 * mm});
            skCircle(sketch, "E353", {"center": v(-12.9, 16.3) * mm, "radius": 0.25 * mm});
            skCircle(sketch, "E354", {"center": v(-6.58, 16.34) * mm, "radius": 0.25 * mm});
            skCircle(sketch, "E355", {"center": v(-5.8, 16.4) * mm, "radius": 0.25 * mm});
            skCircle(sketch, "E356", {"center": v(-4.95, 16.42) * mm, "radius": 0.25 * mm});
            skCircle(sketch, "E357", {"center": v(-4.14, 16.4) * mm, "radius": 0.25 * mm});
            skCircle(sketch, "E358", {"center": v(-7.37, 16.34) * mm, "radius": 0.25 * mm});
            skCircle(sketch, "E359", {"center": v(-1.93, 16.4) * mm, "radius": 0.25 * mm});
            skCircle(sketch, "E360", {"center": v(-3.38, 16.36) * mm, "radius": 0.25 * mm});
            skCircle(sketch, "E361", {"center": v(-1.18, 16.42) * mm, "radius": 0.25 * mm});
            skCircle(sketch, "E362", {"center": v(-2.62, 16.42) * mm, "radius": 0.25 * mm});
            skCircle(sketch, "E363", {"center": v(-8.97, 15.38) * mm, "radius": 0.25 * mm});
            skCircle(sketch, "E364", {"center": v(-9.76, 15.32) * mm, "radius": 0.25 * mm});
            skCircle(sketch, "E365", {"center": v(-10.6, 15.3) * mm, "radius": 0.25 * mm});
            skCircle(sketch, "E366", {"center": v(-11.41, 15.32) * mm, "radius": 0.25 * mm});
            skCircle(sketch, "E367", {"center": v(-8.19, 15.38) * mm, "radius": 0.25 * mm});
            skCircle(sketch, "E368", {"center": v(-13.83, 15.3) * mm, "radius": 0.25 * mm});
            skCircle(sketch, "E369", {"center": v(-12.17, 15.35) * mm, "radius": 0.25 * mm});
            skCircle(sketch, "E370", {"center": v(-14.64, 15.32) * mm, "radius": 0.25 * mm});
            skCircle(sketch, "E371", {"center": v(-0.56, 15.41) * mm, "radius": 0.25 * mm});
            skCircle(sketch, "E372", {"center": v(-12.94, 15.3) * mm, "radius": 0.25 * mm});
            skCircle(sketch, "E373", {"center": v(-6.62, 15.34) * mm, "radius": 0.25 * mm});
            skCircle(sketch, "E374", {"center": v(-5.83, 15.4) * mm, "radius": 0.25 * mm});
            skCircle(sketch, "E375", {"center": v(-5, 15.42) * mm, "radius": 0.25 * mm});
            skCircle(sketch, "E376", {"center": v(-4.18, 15.4) * mm, "radius": 0.25 * mm});
            skCircle(sketch, "E377", {"center": v(-7.4, 15.34) * mm, "radius": 0.25 * mm});
            skCircle(sketch, "E378", {"center": v(-1.98, 15.4) * mm, "radius": 0.25 * mm});
            skCircle(sketch, "E379", {"center": v(-3.42, 15.37) * mm, "radius": 0.25 * mm});
            skCircle(sketch, "E380", {"center": v(-1.22, 15.42) * mm, "radius": 0.25 * mm});
            skCircle(sketch, "E381", {"center": v(-2.66, 15.42) * mm, "radius": 0.25 * mm});
            skCircle(sketch, "E382", {"center": v(-8.81, 24.29) * mm, "radius": 0.25 * mm});
            skCircle(sketch, "E383", {"center": v(-9.6, 24.24) * mm, "radius": 0.25 * mm});
            skCircle(sketch, "E384", {"center": v(-10.44, 24.21) * mm, "radius": 0.25 * mm});
            skCircle(sketch, "E385", {"center": v(-11.25, 24.24) * mm, "radius": 0.25 * mm});
            skCircle(sketch, "E386", {"center": v(-8.03, 24.29) * mm, "radius": 0.25 * mm});
            skCircle(sketch, "E387", {"center": v(-12.01, 24.26) * mm, "radius": 0.25 * mm});
            skCircle(sketch, "E388", {"center": v(-12.77, 24.21) * mm, "radius": 0.25 * mm});
            skCircle(sketch, "E389", {"center": v(-6.46, 24.26) * mm, "radius": 0.25 * mm});
            skCircle(sketch, "E390", {"center": v(-5.67, 24.3) * mm, "radius": 0.25 * mm});
            skCircle(sketch, "E391", {"center": v(-4.83, 24.34) * mm, "radius": 0.25 * mm});
            skCircle(sketch, "E392", {"center": v(-4.02, 24.3) * mm, "radius": 0.25 * mm});
            skCircle(sketch, "E393", {"center": v(-7.25, 24.26) * mm, "radius": 0.25 * mm});
            skCircle(sketch, "E394", {"center": v(-3.26, 24.28) * mm, "radius": 0.25 * mm});
            skCircle(sketch, "E395", {"center": v(-2.38, 24.18) * mm, "radius": 0.25 * mm});
            skCircle(sketch, "E396", {"center": v(-8.89, 23.31) * mm, "radius": 0.25 * mm});
            skCircle(sketch, "E397", {"center": v(-9.67, 23.26) * mm, "radius": 0.25 * mm});
            skCircle(sketch, "E398", {"center": v(-10.51, 23.24) * mm, "radius": 0.25 * mm});
            skCircle(sketch, "E399", {"center": v(-11.33, 23.26) * mm, "radius": 0.25 * mm});
            skCircle(sketch, "E400", {"center": v(-8.1, 23.31) * mm, "radius": 0.25 * mm});
            skCircle(sketch, "E401", {"center": v(-13.74, 23.24) * mm, "radius": 0.25 * mm});
            skCircle(sketch, "E402", {"center": v(-12.09, 23.29) * mm, "radius": 0.25 * mm});
            skCircle(sketch, "E403", {"center": v(-12.85, 23.24) * mm, "radius": 0.25 * mm});
            skCircle(sketch, "E404", {"center": v(-6.54, 23.28) * mm, "radius": 0.25 * mm});
            skCircle(sketch, "E405", {"center": v(-5.75, 23.34) * mm, "radius": 0.25 * mm});
            skCircle(sketch, "E406", {"center": v(-4.9, 23.36) * mm, "radius": 0.25 * mm});
            skCircle(sketch, "E407", {"center": v(-4.1, 23.34) * mm, "radius": 0.25 * mm});
            skCircle(sketch, "E408", {"center": v(-7.32, 23.28) * mm, "radius": 0.25 * mm});
            skCircle(sketch, "E409", {"center": v(-1.9, 23.34) * mm, "radius": 0.25 * mm});
            skCircle(sketch, "E410", {"center": v(-3.33, 23.3) * mm, "radius": 0.25 * mm});
            skCircle(sketch, "E411", {"center": v(-1.3, 23.13) * mm, "radius": 0.25 * mm});
            skCircle(sketch, "E412", {"center": v(-2.57, 23.36) * mm, "radius": 0.25 * mm});
            skCircle(sketch, "E413", {"center": v(-8.89, 22.3) * mm, "radius": 0.25 * mm});
            skCircle(sketch, "E414", {"center": v(-9.67, 22.24) * mm, "radius": 0.25 * mm});
            skCircle(sketch, "E415", {"center": v(-10.51, 22.21) * mm, "radius": 0.25 * mm});
            skCircle(sketch, "E416", {"center": v(-11.33, 22.24) * mm, "radius": 0.25 * mm});
            skCircle(sketch, "E417", {"center": v(-8.1, 22.3) * mm, "radius": 0.25 * mm});
            skCircle(sketch, "E418", {"center": v(-13.74, 22.21) * mm, "radius": 0.25 * mm});
            skCircle(sketch, "E419", {"center": v(-12.09, 22.27) * mm, "radius": 0.25 * mm});
            skCircle(sketch, "E420", {"center": v(-14.36, 22.1) * mm, "radius": 0.25 * mm});
            skCircle(sketch, "E421", {"center": v(-12.85, 22.21) * mm, "radius": 0.25 * mm});
            skCircle(sketch, "E422", {"center": v(-6.54, 22.26) * mm, "radius": 0.25 * mm});
            skCircle(sketch, "E423", {"center": v(-5.75, 22.31) * mm, "radius": 0.25 * mm});
            skCircle(sketch, "E424", {"center": v(-4.9, 22.34) * mm, "radius": 0.25 * mm});
            skCircle(sketch, "E425", {"center": v(-4.1, 22.31) * mm, "radius": 0.25 * mm});
            skCircle(sketch, "E426", {"center": v(-7.32, 22.26) * mm, "radius": 0.25 * mm});
            skCircle(sketch, "E427", {"center": v(-1.9, 22.32) * mm, "radius": 0.25 * mm});
            skCircle(sketch, "E428", {"center": v(-3.33, 22.29) * mm, "radius": 0.25 * mm});
            skCircle(sketch, "E429", {"center": v(-1.13, 22.34) * mm, "radius": 0.25 * mm});
            skCircle(sketch, "E430", {"center": v(-2.57, 22.34) * mm, "radius": 0.25 * mm});
            skCircle(sketch, "E431", {"center": v(-8.89, 21.32) * mm, "radius": 0.25 * mm});
            skCircle(sketch, "E432", {"center": v(-9.67, 21.27) * mm, "radius": 0.25 * mm});
            skCircle(sketch, "E433", {"center": v(-10.51, 21.24) * mm, "radius": 0.25 * mm});
            skCircle(sketch, "E434", {"center": v(-11.33, 21.27) * mm, "radius": 0.25 * mm});
            skCircle(sketch, "E435", {"center": v(-8.1, 21.32) * mm, "radius": 0.25 * mm});
            skCircle(sketch, "E436", {"center": v(-13.74, 21.24) * mm, "radius": 0.25 * mm});
            skCircle(sketch, "E437", {"center": v(-12.09, 21.3) * mm, "radius": 0.25 * mm});
            skCircle(sketch, "E438", {"center": v(-14.55, 21.27) * mm, "radius": 0.25 * mm});
            skCircle(sketch, "E439", {"center": v(-0.48, 21.36) * mm, "radius": 0.25 * mm});
            skCircle(sketch, "E440", {"center": v(-12.85, 21.24) * mm, "radius": 0.25 * mm});
            skCircle(sketch, "E441", {"center": v(-6.54, 21.29) * mm, "radius": 0.25 * mm});
            skCircle(sketch, "E442", {"center": v(-5.75, 21.34) * mm, "radius": 0.25 * mm});
            skCircle(sketch, "E443", {"center": v(-4.9, 21.37) * mm, "radius": 0.25 * mm});
            skCircle(sketch, "E444", {"center": v(-4.1, 21.34) * mm, "radius": 0.25 * mm});
            skCircle(sketch, "E445", {"center": v(-7.32, 21.29) * mm, "radius": 0.25 * mm});
            skCircle(sketch, "E446", {"center": v(-1.9, 21.35) * mm, "radius": 0.25 * mm});
            skCircle(sketch, "E447", {"center": v(-3.33, 21.31) * mm, "radius": 0.25 * mm});
            skCircle(sketch, "E448", {"center": v(-1.13, 21.37) * mm, "radius": 0.25 * mm});
            skCircle(sketch, "E449", {"center": v(-2.57, 21.37) * mm, "radius": 0.25 * mm});
            skCircle(sketch, "E450", {"center": v(-8.93, 20.33) * mm, "radius": 0.25 * mm});
            skCircle(sketch, "E451", {"center": v(-9.72, 20.27) * mm, "radius": 0.25 * mm});
            skCircle(sketch, "E452", {"center": v(-10.56, 20.25) * mm, "radius": 0.25 * mm});
            skCircle(sketch, "E453", {"center": v(-11.37, 20.27) * mm, "radius": 0.25 * mm});
            skCircle(sketch, "E454", {"center": v(-8.14, 20.33) * mm, "radius": 0.25 * mm});
            skCircle(sketch, "E455", {"center": v(-13.78, 20.25) * mm, "radius": 0.25 * mm});
            skCircle(sketch, "E456", {"center": v(-12.13, 20.3) * mm, "radius": 0.25 * mm});
            skCircle(sketch, "E457", {"center": v(-14.6, 20.27) * mm, "radius": 0.25 * mm});
            skCircle(sketch, "E458", {"center": v(-0.52, 20.36) * mm, "radius": 0.25 * mm});
            skCircle(sketch, "E459", {"center": v(-12.9, 20.25) * mm, "radius": 0.25 * mm});
            skCircle(sketch, "E460", {"center": v(-6.58, 20.3) * mm, "radius": 0.25 * mm});
            skCircle(sketch, "E461", {"center": v(-5.79, 20.35) * mm, "radius": 0.25 * mm});
            skCircle(sketch, "E462", {"center": v(-4.95, 20.37) * mm, "radius": 0.25 * mm});
            skCircle(sketch, "E463", {"center": v(-4.14, 20.35) * mm, "radius": 0.25 * mm});
            skCircle(sketch, "E464", {"center": v(-7.36, 20.3) * mm, "radius": 0.25 * mm});
            skCircle(sketch, "E465", {"center": v(-1.93, 20.35) * mm, "radius": 0.25 * mm});
            skCircle(sketch, "E466", {"center": v(-3.38, 20.32) * mm, "radius": 0.25 * mm});
            skCircle(sketch, "E467", {"center": v(-1.18, 20.37) * mm, "radius": 0.25 * mm});
            skCircle(sketch, "E468", {"center": v(-2.62, 20.37) * mm, "radius": 0.25 * mm});
            skCircle(sketch, "E469", {"center": v(-8.93, 25) * mm, "radius": 0.25 * mm});
            skCircle(sketch, "E470", {"center": v(-9.72, 24.95) * mm, "radius": 0.25 * mm});
            skCircle(sketch, "E471", {"center": v(-10.56, 24.93) * mm, "radius": 0.25 * mm});
            skCircle(sketch, "E472", {"center": v(-11.37, 24.95) * mm, "radius": 0.25 * mm});
            skCircle(sketch, "E473", {"center": v(-8.14, 25) * mm, "radius": 0.25 * mm});
            skCircle(sketch, "E474", {"center": v(-6.58, 24.97) * mm, "radius": 0.25 * mm});
            skCircle(sketch, "E475", {"center": v(-5.79, 25.03) * mm, "radius": 0.25 * mm});
            skCircle(sketch, "E476", {"center": v(-4.95, 25.05) * mm, "radius": 0.25 * mm});
            skCircle(sketch, "E477", {"center": v(-4.14, 25.03) * mm, "radius": 0.25 * mm});
            skCircle(sketch, "E478", {"center": v(-7.36, 24.97) * mm, "radius": 0.25 * mm});
            skCircle(sketch, "E479.MirrorC", {"center": v(-8.14, -11.43) * mm, "radius": 0.25 * mm});
            skCircle(sketch, "E480.MirrorC", {"center": v(-9.76, -10.39) * mm, "radius": 0.25 * mm});
            skCircle(sketch, "E481.MirrorC", {"center": v(-1.22, -10.49) * mm, "radius": 0.25 * mm});
            skCircle(sketch, "E482.MirrorC", {"center": v(-3.34, -5.55) * mm, "radius": 0.25 * mm});
            skCircle(sketch, "E483.MirrorC", {"center": v(-7.3, -19.3) * mm, "radius": 0.25 * mm});
            skCircle(sketch, "E484.MirrorC", {"center": v(-4.06, -14.42) * mm, "radius": 0.25 * mm});
            skCircle(sketch, "E485.MirrorC", {"center": v(-6.58, -13.4) * mm, "radius": 0.25 * mm});
            skCircle(sketch, "E486.MirrorC", {"center": v(-12.82, -8.47) * mm, "radius": 0.25 * mm});
            skCircle(sketch, "E487.MirrorC", {"center": v(-14.6, -12.35) * mm, "radius": 0.25 * mm});
            skCircle(sketch, "E488.MirrorC", {"center": v(-11.3, -6.5) * mm, "radius": 0.25 * mm});
            skCircle(sketch, "E489.MirrorC", {"center": v(-12.06, -7.5) * mm, "radius": 0.25 * mm});
            skCircle(sketch, "E490.MirrorC", {"center": v(-8.9, -5.56) * mm, "radius": 0.25 * mm});
            skCircle(sketch, "E491.MirrorC", {"center": v(-10.48, -1.54) * mm, "radius": 0.25 * mm});
            skCircle(sketch, "E492.MirrorC", {"center": v(-2.54, -1.66) * mm, "radius": 0.25 * mm});
            skCircle(sketch, "E493.MirrorC", {"center": v(-1.9, -0.65) * mm, "radius": 0.25 * mm});
            skCircle(sketch, "E494.MirrorC", {"center": v(-4.8, -9.57) * mm, "radius": 0.25 * mm});
            skCircle(sketch, "E495.MirrorC", {"center": v(-0.44, -3.65) * mm, "radius": 0.25 * mm});
            skCircle(sketch, "E496.MirrorC", {"center": v(-13.71, -2.51) * mm, "radius": 0.25 * mm});
            skCircle(sketch, "E497.MirrorC", {"center": v(-4.95, -25.05) * mm, "radius": 0.25 * mm});
            skCircle(sketch, "E498.MirrorC", {"center": v(-3.33, -22.29) * mm, "radius": 0.25 * mm});
            skCircle(sketch, "E499.MirrorC", {"center": v(-4.1, -21.34) * mm, "radius": 0.25 * mm});
            skCircle(sketch, "E500.MirrorC", {"center": v(-6.58, -20.3) * mm, "radius": 0.25 * mm});
            skCircle(sketch, "E501.MirrorC", {"center": v(-1.22, -15.42) * mm, "radius": 0.25 * mm});
            skCircle(sketch, "E502.MirrorC", {"center": v(-8.89, -23.31) * mm, "radius": 0.25 * mm});
            skCircle(sketch, "E503.MirrorC", {"center": v(-2.57, -23.36) * mm, "radius": 0.25 * mm});
            skCircle(sketch, "E504.MirrorC", {"center": v(-6.58, -18.33) * mm, "radius": 0.25 * mm});
            skCircle(sketch, "E505.MirrorC", {"center": v(-14.6, -17.29) * mm, "radius": 0.25 * mm});
            skCircle(sketch, "E506.MirrorC", {"center": v(-8.14, -16.37) * mm, "radius": 0.25 * mm});
            skCircle(sketch, "E507.MirrorC", {"center": v(-9.76, -15.32) * mm, "radius": 0.25 * mm});
            skCircle(sketch, "E508.MirrorC", {"center": v(-11.37, -11.38) * mm, "radius": 0.25 * mm});
            skCircle(sketch, "E509.MirrorC", {"center": v(-8.97, -10.44) * mm, "radius": 0.25 * mm});
            skCircle(sketch, "E510.MirrorC", {"center": v(-3.42, -10.43) * mm, "radius": 0.25 * mm});
            skCircle(sketch, "E511.MirrorC", {"center": v(-4.06, -19.36) * mm, "radius": 0.25 * mm});
            skCircle(sketch, "E512.MirrorC", {"center": v(-4.8, -4.63) * mm, "radius": 0.25 * mm});
            skCircle(sketch, "E513.MirrorC", {"center": v(-5.64, -4.6) * mm, "radius": 0.25 * mm});
            skCircle(sketch, "E514.MirrorC", {"center": v(-6.43, -4.55) * mm, "radius": 0.25 * mm});
            skCircle(sketch, "E515.MirrorC", {"center": v(-12.74, -4.5) * mm, "radius": 0.25 * mm});
            skCircle(sketch, "E516.MirrorC", {"center": v(-0.37, -4.62) * mm, "radius": 0.25 * mm});
            skCircle(sketch, "E517.MirrorC", {"center": v(-14.45, -4.53) * mm, "radius": 0.25 * mm});
            skCircle(sketch, "E518.MirrorC", {"center": v(-11.98, -4.56) * mm, "radius": 0.25 * mm});
            skCircle(sketch, "E519.MirrorC", {"center": v(-13.64, -4.5) * mm, "radius": 0.25 * mm});
            skCircle(sketch, "E520.MirrorC", {"center": v(-8, -4.59) * mm, "radius": 0.25 * mm});
            skCircle(sketch, "E521.MirrorC", {"center": v(-11.22, -4.53) * mm, "radius": 0.25 * mm});
            skCircle(sketch, "E522.MirrorC", {"center": v(-10.4, -4.5) * mm, "radius": 0.25 * mm});
            skCircle(sketch, "E523.MirrorC", {"center": v(-9.57, -4.53) * mm, "radius": 0.25 * mm});
            skCircle(sketch, "E524.MirrorC", {"center": v(-1.9, -5.59) * mm, "radius": 0.25 * mm});
            skCircle(sketch, "E525.MirrorC", {"center": v(-8.78, -4.59) * mm, "radius": 0.25 * mm});
            skCircle(sketch, "E526.MirrorC", {"center": v(-4.88, -14.45) * mm, "radius": 0.25 * mm});
            skCircle(sketch, "E527.MirrorC", {"center": v(-12.9, -13.35) * mm, "radius": 0.25 * mm});
            skCircle(sketch, "E528.MirrorC", {"center": v(-12.13, -12.38) * mm, "radius": 0.25 * mm});
            skCircle(sketch, "E529.MirrorC", {"center": v(-0.44, -8.59) * mm, "radius": 0.25 * mm});
            skCircle(sketch, "E530.MirrorC", {"center": v(-13.71, -7.45) * mm, "radius": 0.25 * mm});
            skCircle(sketch, "E531.MirrorC", {"center": v(-10.48, -6.47) * mm, "radius": 0.25 * mm});
            skCircle(sketch, "E532.MirrorC", {"center": v(-1.78, -4.61) * mm, "radius": 0.25 * mm});
            skCircle(sketch, "E533.MirrorC", {"center": v(-9.64, -1.56) * mm, "radius": 0.25 * mm});
            skCircle(sketch, "E534.MirrorC", {"center": v(-2.54, -6.6) * mm, "radius": 0.25 * mm});
            skCircle(sketch, "E535.MirrorC", {"center": v(-1.1, -1.66) * mm, "radius": 0.25 * mm});
            skCircle(sketch, "E536.MirrorC", {"center": v(-7.33, -0.6) * mm, "radius": 0.25 * mm});
            skCircle(sketch, "E537.MirrorC", {"center": v(-5.64, -9.54) * mm, "radius": 0.25 * mm});
            skCircle(sketch, "E538.MirrorC", {"center": v(-7.22, -4.55) * mm, "radius": 0.25 * mm});
            skCircle(sketch, "E539.MirrorC", {"center": v(-14.52, -3.56) * mm, "radius": 0.25 * mm});
            skCircle(sketch, "E540.MirrorC", {"center": v(-8.07, -2.59) * mm, "radius": 0.25 * mm});
            skCircle(sketch, "E541.MirrorC", {"center": v(-3.99, -4.6) * mm, "radius": 0.25 * mm});
            skCircle(sketch, "E542.MirrorC", {"center": v(-1.9, -22.32) * mm, "radius": 0.25 * mm});
            skCircle(sketch, "E543.MirrorC", {"center": v(-5.79, -25.03) * mm, "radius": 0.25 * mm});
            skCircle(sketch, "E544.MirrorC", {"center": v(-4.9, -21.37) * mm, "radius": 0.25 * mm});
            skCircle(sketch, "E545.MirrorC", {"center": v(-12.9, -20.25) * mm, "radius": 0.25 * mm});
            skCircle(sketch, "E546.MirrorC", {"center": v(-1.3, -23.13) * mm, "radius": 0.25 * mm});
            skCircle(sketch, "E547.MirrorC", {"center": v(-2.38, -24.18) * mm, "radius": 0.25 * mm});
            skCircle(sketch, "E548.MirrorC", {"center": v(-3.42, -15.37) * mm, "radius": 0.25 * mm});
            skCircle(sketch, "E549.MirrorC", {"center": v(-12.13, -17.32) * mm, "radius": 0.25 * mm});
            skCircle(sketch, "E550.MirrorC", {"center": v(-12.9, -18.29) * mm, "radius": 0.25 * mm});
            skCircle(sketch, "E551.MirrorC", {"center": v(-11.37, -16.32) * mm, "radius": 0.25 * mm});
            skCircle(sketch, "E552.MirrorC", {"center": v(-8.97, -15.38) * mm, "radius": 0.25 * mm});
            skCircle(sketch, "E553.MirrorC", {"center": v(-2.62, -11.48) * mm, "radius": 0.25 * mm});
            skCircle(sketch, "E554.MirrorC", {"center": v(-10.56, -11.35) * mm, "radius": 0.25 * mm});
            skCircle(sketch, "E555.MirrorC", {"center": v(-1.98, -10.47) * mm, "radius": 0.25 * mm});
            skCircle(sketch, "E556.MirrorC", {"center": v(-4.88, -19.39) * mm, "radius": 0.25 * mm});
            skCircle(sketch, "E557.MirrorC", {"center": v(-7.33, -5.53) * mm, "radius": 0.25 * mm});
            skCircle(sketch, "E558.MirrorC", {"center": v(-5.72, -14.42) * mm, "radius": 0.25 * mm});
            skCircle(sketch, "E559.MirrorC", {"center": v(-0.52, -13.46) * mm, "radius": 0.25 * mm});
            skCircle(sketch, "E560.MirrorC", {"center": v(-13.79, -12.33) * mm, "radius": 0.25 * mm});
            skCircle(sketch, "E561.MirrorC", {"center": v(-14.52, -8.5) * mm, "radius": 0.25 * mm});
            skCircle(sketch, "E562.MirrorC", {"center": v(-8.07, -7.53) * mm, "radius": 0.25 * mm});
            skCircle(sketch, "E563.MirrorC", {"center": v(-1.1, -6.6) * mm, "radius": 0.25 * mm});
            skCircle(sketch, "E564.MirrorC", {"center": v(-9.64, -6.5) * mm, "radius": 0.25 * mm});
            skCircle(sketch, "E565.MirrorC", {"center": v(-8.86, -1.62) * mm, "radius": 0.25 * mm});
            skCircle(sketch, "E566.MirrorC", {"center": v(-3.3, -1.61) * mm, "radius": 0.25 * mm});
            skCircle(sketch, "E567.MirrorC", {"center": v(-4.1, -0.64) * mm, "radius": 0.25 * mm});
            skCircle(sketch, "E568.MirrorC", {"center": v(-6.43, -9.5) * mm, "radius": 0.25 * mm});
            skCircle(sketch, "E569.MirrorC", {"center": v(-12.06, -3.59) * mm, "radius": 0.25 * mm});
            skCircle(sketch, "E570.MirrorC", {"center": v(-11.3, -2.54) * mm, "radius": 0.25 * mm});
            skCircle(sketch, "E571.MirrorC", {"center": v(-6.58, -24.97) * mm, "radius": 0.25 * mm});
            skCircle(sketch, "E572.MirrorC", {"center": v(-7.32, -22.26) * mm, "radius": 0.25 * mm});
            skCircle(sketch, "E573.MirrorC", {"center": v(-5.75, -21.34) * mm, "radius": 0.25 * mm});
            skCircle(sketch, "E574.MirrorC", {"center": v(-1.98, -15.4) * mm, "radius": 0.25 * mm});
            skCircle(sketch, "E575.MirrorC", {"center": v(-0.52, -20.36) * mm, "radius": 0.25 * mm});
            skCircle(sketch, "E576.MirrorC", {"center": v(-3.33, -23.3) * mm, "radius": 0.25 * mm});
            skCircle(sketch, "E577.MirrorC", {"center": v(-3.26, -24.28) * mm, "radius": 0.25 * mm});
            skCircle(sketch, "E578.MirrorC", {"center": v(-0.52, -18.4) * mm, "radius": 0.25 * mm});
            skCircle(sketch, "E579.MirrorC", {"center": v(-13.79, -17.26) * mm, "radius": 0.25 * mm});
            skCircle(sketch, "E580.MirrorC", {"center": v(-10.56, -16.3) * mm, "radius": 0.25 * mm});
            skCircle(sketch, "E581.MirrorC", {"center": v(-2.62, -16.42) * mm, "radius": 0.25 * mm});
            skCircle(sketch, "E582.MirrorC", {"center": v(-1.18, -11.48) * mm, "radius": 0.25 * mm});
            skCircle(sketch, "E583.MirrorC", {"center": v(-9.72, -11.38) * mm, "radius": 0.25 * mm});
            skCircle(sketch, "E584.MirrorC", {"center": v(-5.72, -19.36) * mm, "radius": 0.25 * mm});
            skCircle(sketch, "E585.MirrorC", {"center": v(-7.4, -10.4) * mm, "radius": 0.25 * mm});
            skCircle(sketch, "E586.MirrorC", {"center": v(-4.1, -5.58) * mm, "radius": 0.25 * mm});
            skCircle(sketch, "E587.MirrorC", {"center": v(-6.5, -14.37) * mm, "radius": 0.25 * mm});
            skCircle(sketch, "E588.MirrorC", {"center": v(-14.6, -13.38) * mm, "radius": 0.25 * mm});
            skCircle(sketch, "E589.MirrorC", {"center": v(-8.14, -12.4) * mm, "radius": 0.25 * mm});
            skCircle(sketch, "E590.MirrorC", {"center": v(-12.06, -8.52) * mm, "radius": 0.25 * mm});
            skCircle(sketch, "E591.MirrorC", {"center": v(-11.3, -7.47) * mm, "radius": 0.25 * mm});
            skCircle(sketch, "E592.MirrorC", {"center": v(-8.86, -6.55) * mm, "radius": 0.25 * mm});
            skCircle(sketch, "E593.MirrorC", {"center": v(-3.3, -6.55) * mm, "radius": 0.25 * mm});
            skCircle(sketch, "E594.MirrorC", {"center": v(-2.54, -2.64) * mm, "radius": 0.25 * mm});
            skCircle(sketch, "E595.MirrorC", {"center": v(-1.86, -1.64) * mm, "radius": 0.25 * mm});
            skCircle(sketch, "E596.MirrorC", {"center": v(-12.74, -9.44) * mm, "radius": 0.25 * mm});
            skCircle(sketch, "E597.MirrorC", {"center": v(-4.92, -0.67) * mm, "radius": 0.25 * mm});
            skCircle(sketch, "E598.MirrorC", {"center": v(-13.71, -3.53) * mm, "radius": 0.25 * mm});
            skCircle(sketch, "E599.MirrorC", {"center": v(-10.48, -2.51) * mm, "radius": 0.25 * mm});
            skCircle(sketch, "E600.MirrorC", {"center": v(-4.1, -22.31) * mm, "radius": 0.25 * mm});
            skCircle(sketch, "E601.MirrorC", {"center": v(-6.54, -21.29) * mm, "radius": 0.25 * mm});
            skCircle(sketch, "E602.MirrorC", {"center": v(-7.4, -15.34) * mm, "radius": 0.25 * mm});
            skCircle(sketch, "E603.MirrorC", {"center": v(-14.6, -20.27) * mm, "radius": 0.25 * mm});
            skCircle(sketch, "E604.MirrorC", {"center": v(-7.25, -24.26) * mm, "radius": 0.25 * mm});
            skCircle(sketch, "E605.MirrorC", {"center": v(-1.9, -23.34) * mm, "radius": 0.25 * mm});
            skCircle(sketch, "E606.MirrorC", {"center": v(-14.6, -18.31) * mm, "radius": 0.25 * mm});
            skCircle(sketch, "E607.MirrorC", {"center": v(-8.14, -17.34) * mm, "radius": 0.25 * mm});
            skCircle(sketch, "E608.MirrorC", {"center": v(-9.72, -16.32) * mm, "radius": 0.25 * mm});
            skCircle(sketch, "E609.MirrorC", {"center": v(-1.18, -16.42) * mm, "radius": 0.25 * mm});
            skCircle(sketch, "E610.MirrorC", {"center": v(-8.93, -11.43) * mm, "radius": 0.25 * mm});
            skCircle(sketch, "E611.MirrorC", {"center": v(-3.38, -11.43) * mm, "radius": 0.25 * mm});
            skCircle(sketch, "E612.MirrorC", {"center": v(-4.18, -10.46) * mm, "radius": 0.25 * mm});
            skCircle(sketch, "E613.MirrorC", {"center": v(-6.5, -19.3) * mm, "radius": 0.25 * mm});
            skCircle(sketch, "E614.MirrorC", {"center": v(-4.92, -5.6) * mm, "radius": 0.25 * mm});
            skCircle(sketch, "E615.MirrorC", {"center": v(-12.82, -14.32) * mm, "radius": 0.25 * mm});
            skCircle(sketch, "E616.MirrorC", {"center": v(-12.13, -13.4) * mm, "radius": 0.25 * mm});
            skCircle(sketch, "E617.MirrorC", {"center": v(-11.37, -12.35) * mm, "radius": 0.25 * mm});
            skCircle(sketch, "E618.MirrorC", {"center": v(-13.71, -8.47) * mm, "radius": 0.25 * mm});
            skCircle(sketch, "E619.MirrorC", {"center": v(-2.54, -7.57) * mm, "radius": 0.25 * mm});
            skCircle(sketch, "E620.MirrorC", {"center": v(-10.48, -7.45) * mm, "radius": 0.25 * mm});
            skCircle(sketch, "E621.MirrorC", {"center": v(-1.86, -6.58) * mm, "radius": 0.25 * mm});
            skCircle(sketch, "E622.MirrorC", {"center": v(-1.1, -2.64) * mm, "radius": 0.25 * mm});
            skCircle(sketch, "E623.MirrorC", {"center": v(-7.3, -1.58) * mm, "radius": 0.25 * mm});
            skCircle(sketch, "E624.MirrorC", {"center": v(-5.76, -0.64) * mm, "radius": 0.25 * mm});
            skCircle(sketch, "E625.MirrorC", {"center": v(-0.37, -9.56) * mm, "radius": 0.25 * mm});
            skCircle(sketch, "E626.MirrorC", {"center": v(-8.14, -25) * mm, "radius": 0.25 * mm});
            skCircle(sketch, "E627.MirrorC", {"center": v(-4.9, -22.34) * mm, "radius": 0.25 * mm});
            skCircle(sketch, "E628.MirrorC", {"center": v(-7.32, -23.28) * mm, "radius": 0.25 * mm});
            skCircle(sketch, "E629.MirrorC", {"center": v(-13.79, -18.29) * mm, "radius": 0.25 * mm});
            skCircle(sketch, "E630.MirrorC", {"center": v(-5.83, -10.46) * mm, "radius": 0.25 * mm});
            skCircle(sketch, "E631.MirrorC", {"center": v(-0.44, -19.38) * mm, "radius": 0.25 * mm});
            skCircle(sketch, "E632.MirrorC", {"center": v(-8.14, -13.43) * mm, "radius": 0.25 * mm});
            skCircle(sketch, "E633.MirrorC", {"center": v(-9.72, -12.35) * mm, "radius": 0.25 * mm});
            skCircle(sketch, "E634.MirrorC", {"center": v(-10.56, -17.26) * mm, "radius": 0.25 * mm});
            skCircle(sketch, "E635.MirrorC", {"center": v(-1.18, -12.45) * mm, "radius": 0.25 * mm});
            skCircle(sketch, "E636.MirrorC", {"center": v(-7.37, -11.4) * mm, "radius": 0.25 * mm});
            skCircle(sketch, "E637.MirrorC", {"center": v(-3.3, -7.52) * mm, "radius": 0.25 * mm});
            skCircle(sketch, "E638.MirrorC", {"center": v(-14.52, -14.35) * mm, "radius": 0.25 * mm});
            skCircle(sketch, "E639.MirrorC", {"center": v(-6.55, -5.53) * mm, "radius": 0.25 * mm});
            skCircle(sketch, "E640.MirrorC", {"center": v(-4.06, -6.57) * mm, "radius": 0.25 * mm});
            skCircle(sketch, "E641.MirrorC", {"center": v(-11.98, -9.5) * mm, "radius": 0.25 * mm});
            skCircle(sketch, "E642.MirrorC", {"center": v(-12.86, -0.54) * mm, "radius": 0.25 * mm});
            skCircle(sketch, "E643.MirrorC", {"center": v(-11.3, -8.5) * mm, "radius": 0.25 * mm});
            skCircle(sketch, "E644.MirrorC", {"center": v(-8.86, -7.53) * mm, "radius": 0.25 * mm});
            skCircle(sketch, "E645.MirrorC", {"center": v(-10.48, -3.53) * mm, "radius": 0.25 * mm});
            skCircle(sketch, "E646.MirrorC", {"center": v(-2.54, -3.66) * mm, "radius": 0.25 * mm});
            skCircle(sketch, "E647.MirrorC", {"center": v(-1.86, -2.62) * mm, "radius": 0.25 * mm});
            skCircle(sketch, "E648.MirrorC", {"center": v(-4.88, -1.66) * mm, "radius": 0.25 * mm});
            skCircle(sketch, "E649.MirrorC", {"center": v(-2.66, -15.42) * mm, "radius": 0.25 * mm});
            skCircle(sketch, "E650.MirrorC", {"center": v(-10.56, -24.93) * mm, "radius": 0.25 * mm});
            skCircle(sketch, "E651.MirrorC", {"center": v(-13.78, -20.25) * mm, "radius": 0.25 * mm});
            skCircle(sketch, "E652.MirrorC", {"center": v(-4.1, -23.34) * mm, "radius": 0.25 * mm});
            skCircle(sketch, "E653.MirrorC", {"center": v(-0.48, -21.36) * mm, "radius": 0.25 * mm});
            skCircle(sketch, "E654.MirrorC", {"center": v(-5.75, -22.31) * mm, "radius": 0.25 * mm});
            skCircle(sketch, "E655.MirrorC", {"center": v(-2.62, -17.39) * mm, "radius": 0.25 * mm});
            skCircle(sketch, "E656.MirrorC", {"center": v(-1.93, -16.4) * mm, "radius": 0.25 * mm});
            skCircle(sketch, "E657.MirrorC", {"center": v(-4.83, -24.34) * mm, "radius": 0.25 * mm});
            skCircle(sketch, "E658.MirrorC", {"center": v(-5, -15.42) * mm, "radius": 0.25 * mm});
            skCircle(sketch, "E659.MirrorC", {"center": v(-7.36, -24.97) * mm, "radius": 0.25 * mm});
            skCircle(sketch, "E660.MirrorC", {"center": v(-8.93, -12.4) * mm, "radius": 0.25 * mm});
            skCircle(sketch, "E661.MirrorC", {"center": v(-11.37, -13.38) * mm, "radius": 0.25 * mm});
            skCircle(sketch, "E662.MirrorC", {"center": v(-4.14, -11.45) * mm, "radius": 0.25 * mm});
            skCircle(sketch, "E663.MirrorC", {"center": v(-3.38, -12.4) * mm, "radius": 0.25 * mm});
            skCircle(sketch, "E664.MirrorC", {"center": v(-12.06, -14.38) * mm, "radius": 0.25 * mm});
            skCircle(sketch, "E665.MirrorC", {"center": v(-1.86, -7.55) * mm, "radius": 0.25 * mm});
            skCircle(sketch, "E666.MirrorC", {"center": v(-4.88, -6.6) * mm, "radius": 0.25 * mm});
            skCircle(sketch, "E667.MirrorC", {"center": v(-13.64, -9.44) * mm, "radius": 0.25 * mm});
            skCircle(sketch, "E668.MirrorC", {"center": v(-12.86, -5.48) * mm, "radius": 0.25 * mm});
            skCircle(sketch, "E669.MirrorC", {"center": v(-0.49, -0.66) * mm, "radius": 0.25 * mm});
            skCircle(sketch, "E670.MirrorC", {"center": v(-10.48, -8.47) * mm, "radius": 0.25 * mm});
            skCircle(sketch, "E671.MirrorC", {"center": v(-2.54, -8.6) * mm, "radius": 0.25 * mm});
            skCircle(sketch, "E672.MirrorC", {"center": v(-9.64, -3.56) * mm, "radius": 0.25 * mm});
            skCircle(sketch, "E673.MirrorC", {"center": v(-2.57, -22.34) * mm, "radius": 0.25 * mm});
            skCircle(sketch, "E674.MirrorC", {"center": v(-1.1, -3.66) * mm, "radius": 0.25 * mm});
            skCircle(sketch, "E675.MirrorC", {"center": v(-4.95, -20.37) * mm, "radius": 0.25 * mm});
            skCircle(sketch, "E676.MirrorC", {"center": v(-8.81, -24.29) * mm, "radius": 0.25 * mm});
            skCircle(sketch, "E677.MirrorC", {"center": v(-10.51, -23.24) * mm, "radius": 0.25 * mm});
            skCircle(sketch, "E678.MirrorC", {"center": v(-9.67, -22.24) * mm, "radius": 0.25 * mm});
            skCircle(sketch, "E679.MirrorC", {"center": v(-7.3, -2.56) * mm, "radius": 0.25 * mm});
            skCircle(sketch, "E680.MirrorC", {"center": v(-5.72, -1.64) * mm, "radius": 0.25 * mm});
            skCircle(sketch, "E681.MirrorC", {"center": v(-4.14, -25.03) * mm, "radius": 0.25 * mm});
            skCircle(sketch, "E682.MirrorC", {"center": v(-14.55, -21.27) * mm, "radius": 0.25 * mm});
            skCircle(sketch, "E683.MirrorC", {"center": v(-8.14, -20.33) * mm, "radius": 0.25 * mm});
            skCircle(sketch, "E684.MirrorC", {"center": v(-6.54, -22.26) * mm, "radius": 0.25 * mm});
            skCircle(sketch, "E685.MirrorC", {"center": v(-9.72, -24.95) * mm, "radius": 0.25 * mm});
            skCircle(sketch, "E686.MirrorC", {"center": v(-1.18, -17.39) * mm, "radius": 0.25 * mm});
            skCircle(sketch, "E687.MirrorC", {"center": v(-4.9, -23.36) * mm, "radius": 0.25 * mm});
            skCircle(sketch, "E688.MirrorC", {"center": v(-5.83, -15.4) * mm, "radius": 0.25 * mm});
            skCircle(sketch, "E689.MirrorC", {"center": v(-7.37, -16.34) * mm, "radius": 0.25 * mm});
            skCircle(sketch, "E690.MirrorC", {"center": v(-6.62, -10.4) * mm, "radius": 0.25 * mm});
            skCircle(sketch, "E691.MirrorC", {"center": v(-5.67, -24.3) * mm, "radius": 0.25 * mm});
            skCircle(sketch, "E692.MirrorC", {"center": v(-14.52, -19.29) * mm, "radius": 0.25 * mm});
            skCircle(sketch, "E693.MirrorC", {"center": v(-9.72, -17.29) * mm, "radius": 0.25 * mm});
            skCircle(sketch, "E694.MirrorC", {"center": v(-8.14, -18.36) * mm, "radius": 0.25 * mm});
            skCircle(sketch, "E695.MirrorC", {"center": v(-8.93, -16.37) * mm, "radius": 0.25 * mm});
            skCircle(sketch, "E696.MirrorC", {"center": v(-3.38, -16.36) * mm, "radius": 0.25 * mm});
            skCircle(sketch, "E697.MirrorC", {"center": v(-4.18, -15.4) * mm, "radius": 0.25 * mm});
            skCircle(sketch, "E698.MirrorC", {"center": v(-7.3, -7.5) * mm, "radius": 0.25 * mm});
            skCircle(sketch, "E699.MirrorC", {"center": v(-5.72, -6.57) * mm, "radius": 0.25 * mm});
            skCircle(sketch, "E700.MirrorC", {"center": v(-13.71, -14.32) * mm, "radius": 0.25 * mm});
            skCircle(sketch, "E701.MirrorC", {"center": v(-0.49, -5.6) * mm, "radius": 0.25 * mm});
            skCircle(sketch, "E702.MirrorC", {"center": v(-8, -9.52) * mm, "radius": 0.25 * mm});
            skCircle(sketch, "E703.MirrorC", {"center": v(-14.57, -0.57) * mm, "radius": 0.25 * mm});
            skCircle(sketch, "E704.MirrorC", {"center": v(-9.64, -8.5) * mm, "radius": 0.25 * mm});
            skCircle(sketch, "E705.MirrorC", {"center": v(-1.1, -8.6) * mm, "radius": 0.25 * mm});
            skCircle(sketch, "E706.MirrorC", {"center": v(-3.3, -3.6) * mm, "radius": 0.25 * mm});
            skCircle(sketch, "E707.MirrorC", {"center": v(-8.86, -3.61) * mm, "radius": 0.25 * mm});
            skCircle(sketch, "E708.MirrorC", {"center": v(-4.06, -2.6) * mm, "radius": 0.25 * mm});
            skCircle(sketch, "E709.MirrorC", {"center": v(-6.5, -1.58) * mm, "radius": 0.25 * mm});
            skCircle(sketch, "E710.MirrorC", {"center": v(-5, -10.49) * mm, "radius": 0.25 * mm});
            skCircle(sketch, "E711.MirrorC", {"center": v(-1.9, -21.35) * mm, "radius": 0.25 * mm});
            skCircle(sketch, "E712.MirrorC", {"center": v(-4.02, -24.3) * mm, "radius": 0.25 * mm});
            skCircle(sketch, "E713.MirrorC", {"center": v(-12.09, -21.3) * mm, "radius": 0.25 * mm});
            skCircle(sketch, "E714.MirrorC", {"center": v(-8.93, -25) * mm, "radius": 0.25 * mm});
            skCircle(sketch, "E715.MirrorC", {"center": v(-12.85, -22.21) * mm, "radius": 0.25 * mm});
            skCircle(sketch, "E716.MirrorC", {"center": v(-11.37, -20.27) * mm, "radius": 0.25 * mm});
            skCircle(sketch, "E717.MirrorC", {"center": v(-5.75, -23.34) * mm, "radius": 0.25 * mm});
            skCircle(sketch, "E718.MirrorC", {"center": v(-3.38, -17.34) * mm, "radius": 0.25 * mm});
            skCircle(sketch, "E719.MirrorC", {"center": v(-6.62, -15.34) * mm, "radius": 0.25 * mm});
            skCircle(sketch, "E720.MirrorC", {"center": v(-4.14, -16.4) * mm, "radius": 0.25 * mm});
            skCircle(sketch, "E721.MirrorC", {"center": v(-12.94, -10.36) * mm, "radius": 0.25 * mm});
            skCircle(sketch, "E722.MirrorC", {"center": v(-6.46, -24.26) * mm, "radius": 0.25 * mm});
            skCircle(sketch, "E723.MirrorC", {"center": v(-11.37, -18.31) * mm, "radius": 0.25 * mm});
            skCircle(sketch, "E724.MirrorC", {"center": v(-12.06, -19.31) * mm, "radius": 0.25 * mm});
            skCircle(sketch, "E725.MirrorC", {"center": v(-8.93, -17.34) * mm, "radius": 0.25 * mm});
            skCircle(sketch, "E726.MirrorC", {"center": v(-10.56, -13.35) * mm, "radius": 0.25 * mm});
            skCircle(sketch, "E727.MirrorC", {"center": v(-2.62, -13.47) * mm, "radius": 0.25 * mm});
            skCircle(sketch, "E728.MirrorC", {"center": v(-1.93, -12.43) * mm, "radius": 0.25 * mm});
            skCircle(sketch, "E729.MirrorC", {"center": v(-4.95, -11.48) * mm, "radius": 0.25 * mm});
            skCircle(sketch, "E730.MirrorC", {"center": v(-12.1, -0.6) * mm, "radius": 0.25 * mm});
            skCircle(sketch, "E731.MirrorC", {"center": v(-11.22, -9.47) * mm, "radius": 0.25 * mm});
            skCircle(sketch, "E732.MirrorC", {"center": v(-8.86, -8.55) * mm, "radius": 0.25 * mm});
            skCircle(sketch, "E733.MirrorC", {"center": v(-3.3, -8.54) * mm, "radius": 0.25 * mm});
            skCircle(sketch, "E734.MirrorC", {"center": v(-2.47, -4.63) * mm, "radius": 0.25 * mm});
            skCircle(sketch, "E735.MirrorC", {"center": v(-1.86, -3.64) * mm, "radius": 0.25 * mm});
            skCircle(sketch, "E736.MirrorC", {"center": v(-4.88, -2.64) * mm, "radius": 0.25 * mm});
            skCircle(sketch, "E737.MirrorC", {"center": v(-12.82, -1.54) * mm, "radius": 0.25 * mm});
            skCircle(sketch, "E738.MirrorC", {"center": v(-12.82, -19.26) * mm, "radius": 0.25 * mm});
            skCircle(sketch, "E739.MirrorC", {"center": v(-11.37, -17.29) * mm, "radius": 0.25 * mm});
            skCircle(sketch, "E740.MirrorC", {"center": v(-13.74, -21.24) * mm, "radius": 0.25 * mm});
            skCircle(sketch, "E741.MirrorC", {"center": v(-2.62, -20.37) * mm, "radius": 0.25 * mm});
            skCircle(sketch, "E742.MirrorC", {"center": v(-10.56, -20.25) * mm, "radius": 0.25 * mm});
            skCircle(sketch, "E743.MirrorC", {"center": v(-14.36, -22.1) * mm, "radius": 0.25 * mm});
            skCircle(sketch, "E744.MirrorC", {"center": v(-4.95, -18.41) * mm, "radius": 0.25 * mm});
            skCircle(sketch, "E745.MirrorC", {"center": v(-6.54, -23.28) * mm, "radius": 0.25 * mm});
            skCircle(sketch, "E746.MirrorC", {"center": v(-1.93, -17.37) * mm, "radius": 0.25 * mm});
            skCircle(sketch, "E747.MirrorC", {"center": v(-4.95, -16.42) * mm, "radius": 0.25 * mm});
            skCircle(sketch, "E748.MirrorC", {"center": v(-12.94, -15.3) * mm, "radius": 0.25 * mm});
            skCircle(sketch, "E749.MirrorC", {"center": v(-12.77, -24.21) * mm, "radius": 0.25 * mm});
            skCircle(sketch, "E750.MirrorC", {"center": v(-9.67, -23.26) * mm, "radius": 0.25 * mm});
            skCircle(sketch, "E751.MirrorC", {"center": v(-0.56, -10.48) * mm, "radius": 0.25 * mm});
            skCircle(sketch, "E752.MirrorC", {"center": v(-13.71, -19.26) * mm, "radius": 0.25 * mm});
            skCircle(sketch, "E753.MirrorC", {"center": v(-12.9, -17.26) * mm, "radius": 0.25 * mm});
            skCircle(sketch, "E754.MirrorC", {"center": v(-10.56, -18.29) * mm, "radius": 0.25 * mm});
            skCircle(sketch, "E755.MirrorC", {"center": v(-1.18, -13.47) * mm, "radius": 0.25 * mm});
            skCircle(sketch, "E756.MirrorC", {"center": v(-9.72, -13.38) * mm, "radius": 0.25 * mm});
            skCircle(sketch, "E757.MirrorC", {"center": v(-2.62, -18.41) * mm, "radius": 0.25 * mm});
            skCircle(sketch, "E758.MirrorC", {"center": v(-7.37, -12.37) * mm, "radius": 0.25 * mm});
            skCircle(sketch, "E759.MirrorC", {"center": v(-5.8, -11.45) * mm, "radius": 0.25 * mm});
            skCircle(sketch, "E760.MirrorC", {"center": v(-4.06, -7.55) * mm, "radius": 0.25 * mm});
            skCircle(sketch, "E761.MirrorC", {"center": v(-6.5, -6.52) * mm, "radius": 0.25 * mm});
            skCircle(sketch, "E762.MirrorC", {"center": v(-14.57, -5.5) * mm, "radius": 0.25 * mm});
            skCircle(sketch, "E763.MirrorC", {"center": v(-8.07, -14.4) * mm, "radius": 0.25 * mm});
            skCircle(sketch, "E764.MirrorC", {"center": v(-1.03, -4.63) * mm, "radius": 0.25 * mm});
            skCircle(sketch, "E765.MirrorC", {"center": v(-7.3, -3.58) * mm, "radius": 0.25 * mm});
            skCircle(sketch, "E766.MirrorC", {"center": v(-5.72, -2.6) * mm, "radius": 0.25 * mm});
            skCircle(sketch, "E767.MirrorC", {"center": v(-0.44, -1.65) * mm, "radius": 0.25 * mm});
            skCircle(sketch, "E768.MirrorC", {"center": v(-12.13, -16.34) * mm, "radius": 0.25 * mm});
            skCircle(sketch, "E769.MirrorC", {"center": v(-13.79, -11.35) * mm, "radius": 0.25 * mm});
            skCircle(sketch, "E770.MirrorC", {"center": v(-11.41, -15.32) * mm, "radius": 0.25 * mm});
            skCircle(sketch, "E771.MirrorC", {"center": v(-10.6, -10.36) * mm, "radius": 0.25 * mm});
            skCircle(sketch, "E772.MirrorC", {"center": v(-1.86, -19.37) * mm, "radius": 0.25 * mm});
            skCircle(sketch, "E773.MirrorC", {"center": v(-2.66, -10.49) * mm, "radius": 0.25 * mm});
            skCircle(sketch, "E774.MirrorC", {"center": v(-1.14, -5.6) * mm, "radius": 0.25 * mm});
            skCircle(sketch, "E775.MirrorC", {"center": v(-8.1, -21.32) * mm, "radius": 0.25 * mm});
            skCircle(sketch, "E776.MirrorC", {"center": v(-9.72, -20.27) * mm, "radius": 0.25 * mm});
            skCircle(sketch, "E777.MirrorC", {"center": v(-1.18, -20.37) * mm, "radius": 0.25 * mm});
            skCircle(sketch, "E778.MirrorC", {"center": v(-12.85, -23.24) * mm, "radius": 0.25 * mm});
            skCircle(sketch, "E779.MirrorC", {"center": v(-12.09, -22.27) * mm, "radius": 0.25 * mm});
            skCircle(sketch, "E780.MirrorC", {"center": v(-7.37, -17.31) * mm, "radius": 0.25 * mm});
            skCircle(sketch, "E781.MirrorC", {"center": v(-5.8, -16.4) * mm, "radius": 0.25 * mm});
            skCircle(sketch, "E782.MirrorC", {"center": v(-12.13, -18.34) * mm, "radius": 0.25 * mm});
            skCircle(sketch, "E783.MirrorC", {"center": v(-0.56, -15.41) * mm, "radius": 0.25 * mm});
            skCircle(sketch, "E784.MirrorC", {"center": v(-12.01, -24.26) * mm, "radius": 0.25 * mm});
            skCircle(sketch, "E785.MirrorC", {"center": v(-14.64, -10.39) * mm, "radius": 0.25 * mm});
            skCircle(sketch, "E786.MirrorC", {"center": v(-8.07, -19.34) * mm, "radius": 0.25 * mm});
            skCircle(sketch, "E787.MirrorC", {"center": v(-7.3, -14.37) * mm, "radius": 0.25 * mm});
            skCircle(sketch, "E788.MirrorC", {"center": v(-0.52, -12.44) * mm, "radius": 0.25 * mm});
            skCircle(sketch, "E789.MirrorC", {"center": v(-13.79, -13.35) * mm, "radius": 0.25 * mm});
            skCircle(sketch, "E790.MirrorC", {"center": v(-9.72, -18.31) * mm, "radius": 0.25 * mm});
            skCircle(sketch, "E791.MirrorC", {"center": v(-1.18, -18.41) * mm, "radius": 0.25 * mm});
            skCircle(sketch, "E792.MirrorC", {"center": v(-8.93, -13.43) * mm, "radius": 0.25 * mm});
            skCircle(sketch, "E793.MirrorC", {"center": v(-3.38, -13.42) * mm, "radius": 0.25 * mm});
            skCircle(sketch, "E794.MirrorC", {"center": v(-5.8, -13.45) * mm, "radius": 0.25 * mm});
            skCircle(sketch, "E795.MirrorC", {"center": v(-4.14, -12.43) * mm, "radius": 0.25 * mm});
            skCircle(sketch, "E796.MirrorC", {"center": v(-6.58, -11.4) * mm, "radius": 0.25 * mm});
            skCircle(sketch, "E797.MirrorC", {"center": v(-12.82, -6.47) * mm, "radius": 0.25 * mm});
            skCircle(sketch, "E798.MirrorC", {"center": v(-4.88, -7.57) * mm, "radius": 0.25 * mm});
            skCircle(sketch, "E799.MirrorC", {"center": v(-12.1, -5.53) * mm, "radius": 0.25 * mm});
            skCircle(sketch, "E800.MirrorC", {"center": v(-11.3, -14.35) * mm, "radius": 0.25 * mm});
            skCircle(sketch, "E801.MirrorC", {"center": v(-13.75, -0.54) * mm, "radius": 0.25 * mm});
            skCircle(sketch, "E802.MirrorC", {"center": v(-10.4, -9.44) * mm, "radius": 0.25 * mm});
            skCircle(sketch, "E803.MirrorC", {"center": v(-2.47, -9.57) * mm, "radius": 0.25 * mm});
            skCircle(sketch, "E804.MirrorC", {"center": v(-1.86, -8.58) * mm, "radius": 0.25 * mm});
            skCircle(sketch, "E805.MirrorC", {"center": v(-8.93, -20.33) * mm, "radius": 0.25 * mm});
            skCircle(sketch, "E806.MirrorC", {"center": v(-12.06, -1.6) * mm, "radius": 0.25 * mm});
            skCircle(sketch, "E807.MirrorC", {"center": v(-4.06, -8.57) * mm, "radius": 0.25 * mm});
            skCircle(sketch, "E808.MirrorC", {"center": v(-12.09, -23.29) * mm, "radius": 0.25 * mm});
            skCircle(sketch, "E809.MirrorC", {"center": v(-4.14, -17.36) * mm, "radius": 0.25 * mm});
            skCircle(sketch, "E810.MirrorC", {"center": v(-13.74, -22.21) * mm, "radius": 0.25 * mm});
            skCircle(sketch, "E811.MirrorC", {"center": v(-7.3, -6.52) * mm, "radius": 0.25 * mm});
            skCircle(sketch, "E812.MirrorC", {"center": v(-8.19, -10.44) * mm, "radius": 0.25 * mm});
            skCircle(sketch, "E813.MirrorC", {"center": v(-2.57, -21.37) * mm, "radius": 0.25 * mm});
            skCircle(sketch, "E814.MirrorC", {"center": v(-8.1, -22.3) * mm, "radius": 0.25 * mm});
            skCircle(sketch, "E815.MirrorC", {"center": v(-6.5, -3.58) * mm, "radius": 0.25 * mm});
            skCircle(sketch, "E816.MirrorC", {"center": v(-0.52, -17.38) * mm, "radius": 0.25 * mm});
            skCircle(sketch, "E817.MirrorC", {"center": v(-4.95, -12.45) * mm, "radius": 0.25 * mm});
            skCircle(sketch, "E818.MirrorC", {"center": v(-12.9, -11.35) * mm, "radius": 0.25 * mm});
            skCircle(sketch, "E819.MirrorC", {"center": v(-5.72, -7.55) * mm, "radius": 0.25 * mm});
            skCircle(sketch, "E820.MirrorC", {"center": v(-0.44, -6.6) * mm, "radius": 0.25 * mm});
            skCircle(sketch, "E821.MirrorC", {"center": v(-2.54, -14.45) * mm, "radius": 0.25 * mm});
            skCircle(sketch, "E822.MirrorC", {"center": v(-8.19, -15.38) * mm, "radius": 0.25 * mm});
            skCircle(sketch, "E823.MirrorC", {"center": v(-11.41, -10.39) * mm, "radius": 0.25 * mm});
            skCircle(sketch, "E824.MirrorC", {"center": v(-5.8, -12.43) * mm, "radius": 0.25 * mm});
            skCircle(sketch, "E825.MirrorC", {"center": v(-0.52, -11.47) * mm, "radius": 0.25 * mm});
            skCircle(sketch, "E826.MirrorC", {"center": v(-8.11, -5.56) * mm, "radius": 0.25 * mm});
            skCircle(sketch, "E827.MirrorC", {"center": v(-12.82, -3.53) * mm, "radius": 0.25 * mm});
            skCircle(sketch, "E828.MirrorC", {"center": v(-1.93, -18.4) * mm, "radius": 0.25 * mm});
            skCircle(sketch, "E829.MirrorC", {"center": v(-1.78, -9.55) * mm, "radius": 0.25 * mm});
            skCircle(sketch, "E830.MirrorC", {"center": v(-10.52, -0.54) * mm, "radius": 0.25 * mm});
            skCircle(sketch, "E831.MirrorC", {"center": v(-10.51, -21.24) * mm, "radius": 0.25 * mm});
            skCircle(sketch, "E832.MirrorC", {"center": v(-13.74, -23.24) * mm, "radius": 0.25 * mm});
            skCircle(sketch, "E833.MirrorC", {"center": v(-10.44, -24.21) * mm, "radius": 0.25 * mm});
            skCircle(sketch, "E834.MirrorC", {"center": v(-13.83, -15.3) * mm, "radius": 0.25 * mm});
            skCircle(sketch, "E835.MirrorC", {"center": v(-0.52, -16.4) * mm, "radius": 0.25 * mm});
            skCircle(sketch, "E836.MirrorC", {"center": v(-4.88, -8.6) * mm, "radius": 0.25 * mm});
            skCircle(sketch, "E837.MirrorC", {"center": v(-8.86, -14.4) * mm, "radius": 0.25 * mm});
            skCircle(sketch, "E838.MirrorC", {"center": v(-8.89, -21.32) * mm, "radius": 0.25 * mm});
            skCircle(sketch, "E839.MirrorC", {"center": v(-4.14, -20.35) * mm, "radius": 0.25 * mm});
            skCircle(sketch, "E840.MirrorC", {"center": v(-10.51, -22.21) * mm, "radius": 0.25 * mm});
            skCircle(sketch, "E841.MirrorC", {"center": v(-1.1, -14.45) * mm, "radius": 0.25 * mm});
            skCircle(sketch, "E842.MirrorC", {"center": v(-7.37, -13.4) * mm, "radius": 0.25 * mm});
            skCircle(sketch, "E843.MirrorC", {"center": v(-6.5, -7.5) * mm, "radius": 0.25 * mm});
            skCircle(sketch, "E844.MirrorC", {"center": v(-8.07, -1.62) * mm, "radius": 0.25 * mm});
            skCircle(sketch, "E845.MirrorC", {"center": v(-14.52, -2.54) * mm, "radius": 0.25 * mm});
            skCircle(sketch, "E846.MirrorC", {"center": v(-1.93, -20.35) * mm, "radius": 0.25 * mm});
            skCircle(sketch, "E847.MirrorC", {"center": v(-5.72, -8.57) * mm, "radius": 0.25 * mm});
            skCircle(sketch, "E848.MirrorC", {"center": v(-1.13, -22.34) * mm, "radius": 0.25 * mm});
            skCircle(sketch, "E849.MirrorC", {"center": v(-13.75, -5.48) * mm, "radius": 0.25 * mm});
            skCircle(sketch, "E850.MirrorC", {"center": v(-3.34, -0.62) * mm, "radius": 0.25 * mm});
            skCircle(sketch, "E851.MirrorC", {"center": v(-9.57, -9.47) * mm, "radius": 0.25 * mm});
            skCircle(sketch, "E852.MirrorC", {"center": v(-1.93, -13.46) * mm, "radius": 0.25 * mm});
            skCircle(sketch, "E853.MirrorC", {"center": v(-8.9, -0.62) * mm, "radius": 0.25 * mm});
            skCircle(sketch, "E854.MirrorC", {"center": v(-6.58, -16.34) * mm, "radius": 0.25 * mm});
            skCircle(sketch, "E855.MirrorC", {"center": v(-10.56, -12.33) * mm, "radius": 0.25 * mm});
            skCircle(sketch, "E856.MirrorC", {"center": v(-8.03, -24.29) * mm, "radius": 0.25 * mm});
            skCircle(sketch, "E857.MirrorC", {"center": v(-3.38, -20.32) * mm, "radius": 0.25 * mm});
            skCircle(sketch, "E858.MirrorC", {"center": v(-6.5, -8.52) * mm, "radius": 0.25 * mm});
            skCircle(sketch, "E859.MirrorC", {"center": v(-1.1, -7.57) * mm, "radius": 0.25 * mm});
            skCircle(sketch, "E860.MirrorC", {"center": v(-11.33, -22.24) * mm, "radius": 0.25 * mm});
            skCircle(sketch, "E861.MirrorC", {"center": v(-8.1, -23.31) * mm, "radius": 0.25 * mm});
            skCircle(sketch, "E862.MirrorC", {"center": v(-3.3, -19.33) * mm, "radius": 0.25 * mm});
            skCircle(sketch, "E863.MirrorC", {"center": v(-4.14, -18.38) * mm, "radius": 0.25 * mm});
            skCircle(sketch, "E864.MirrorC", {"center": v(-9.6, -24.24) * mm, "radius": 0.25 * mm});
            skCircle(sketch, "E865.MirrorC", {"center": v(-3.3, -14.4) * mm, "radius": 0.25 * mm});
            skCircle(sketch, "E866.MirrorC", {"center": v(-4.14, -13.45) * mm, "radius": 0.25 * mm});
            skCircle(sketch, "E867.MirrorC", {"center": v(-7.37, -18.33) * mm, "radius": 0.25 * mm});
            skCircle(sketch, "E868.MirrorC", {"center": v(-9.64, -19.29) * mm, "radius": 0.25 * mm});
            skCircle(sketch, "E869.MirrorC", {"center": v(-3.23, -9.52) * mm, "radius": 0.25 * mm});
            skCircle(sketch, "E870.MirrorC", {"center": v(-4.88, -3.66) * mm, "radius": 0.25 * mm});
            skCircle(sketch, "E871.MirrorC", {"center": v(-12.82, -2.51) * mm, "radius": 0.25 * mm});
            skCircle(sketch, "E872.MirrorC", {"center": v(-12.06, -2.56) * mm, "radius": 0.25 * mm});
            skCircle(sketch, "E873.MirrorC", {"center": v(-8.78, -9.52) * mm, "radius": 0.25 * mm});
            skCircle(sketch, "E874.MirrorC", {"center": v(-11.34, -0.57) * mm, "radius": 0.25 * mm});
            skCircle(sketch, "E875.MirrorC", {"center": v(-14.52, -6.5) * mm, "radius": 0.25 * mm});
            skCircle(sketch, "E876.MirrorC", {"center": v(-9.64, -14.35) * mm, "radius": 0.25 * mm});
            skCircle(sketch, "E877.MirrorC", {"center": v(-3.99, -9.54) * mm, "radius": 0.25 * mm});
            skCircle(sketch, "E878.MirrorC", {"center": v(-7.36, -20.3) * mm, "radius": 0.25 * mm});
            skCircle(sketch, "E879.MirrorC", {"center": v(-1.13, -21.37) * mm, "radius": 0.25 * mm});
            skCircle(sketch, "E880.MirrorC", {"center": v(-5.79, -20.35) * mm, "radius": 0.25 * mm});
            skCircle(sketch, "E881.MirrorC", {"center": v(-13.79, -16.3) * mm, "radius": 0.25 * mm});
            skCircle(sketch, "E882.MirrorC", {"center": v(-7.32, -21.29) * mm, "radius": 0.25 * mm});
            skCircle(sketch, "E883.MirrorC", {"center": v(-11.33, -23.26) * mm, "radius": 0.25 * mm});
            skCircle(sketch, "E884.MirrorC", {"center": v(-7.22, -9.5) * mm, "radius": 0.25 * mm});
            skCircle(sketch, "E885.MirrorC", {"center": v(-6.5, -2.56) * mm, "radius": 0.25 * mm});
            skCircle(sketch, "E886.MirrorC", {"center": v(-3.23, -4.58) * mm, "radius": 0.25 * mm});
            skCircle(sketch, "E887.MirrorC", {"center": v(-4.06, -3.63) * mm, "radius": 0.25 * mm});
            skCircle(sketch, "E888.MirrorC", {"center": v(-7.3, -8.52) * mm, "radius": 0.25 * mm});
            skCircle(sketch, "E889.MirrorC", {"center": v(-1.03, -9.57) * mm, "radius": 0.25 * mm});
            skCircle(sketch, "E890.MirrorC", {"center": v(-11.25, -24.24) * mm, "radius": 0.25 * mm});
            skCircle(sketch, "E891.MirrorC", {"center": v(-10.48, -19.26) * mm, "radius": 0.25 * mm});
            skCircle(sketch, "E892.MirrorC", {"center": v(-13.83, -10.36) * mm, "radius": 0.25 * mm});
            skCircle(sketch, "E893.MirrorC", {"center": v(-2.54, -19.39) * mm, "radius": 0.25 * mm});
            skCircle(sketch, "E894.MirrorC", {"center": v(-5.8, -18.38) * mm, "radius": 0.25 * mm});
            skCircle(sketch, "E895.MirrorC", {"center": v(-12.9, -16.3) * mm, "radius": 0.25 * mm});
            skCircle(sketch, "E896.MirrorC", {"center": v(-4.95, -17.39) * mm, "radius": 0.25 * mm});
            skCircle(sketch, "E897.MirrorC", {"center": v(-12.17, -15.35) * mm, "radius": 0.25 * mm});
            skCircle(sketch, "E898.MirrorC", {"center": v(-14.52, -1.56) * mm, "radius": 0.25 * mm});
            skCircle(sketch, "E899.MirrorC", {"center": v(-3.38, -18.36) * mm, "radius": 0.25 * mm});
            skCircle(sketch, "E900.MirrorC", {"center": v(-11.3, -19.29) * mm, "radius": 0.25 * mm});
            skCircle(sketch, "E901.MirrorC", {"center": v(-12.17, -10.41) * mm, "radius": 0.25 * mm});
            skCircle(sketch, "E902.MirrorC", {"center": v(-8.93, -18.36) * mm, "radius": 0.25 * mm});
            skCircle(sketch, "E903.MirrorC", {"center": v(-14.64, -15.32) * mm, "radius": 0.25 * mm});
            skCircle(sketch, "E904.MirrorC", {"center": v(-2.62, -12.45) * mm, "radius": 0.25 * mm});
            skCircle(sketch, "E905.MirrorC", {"center": v(-11.33, -21.27) * mm, "radius": 0.25 * mm});
            skCircle(sketch, "E906.MirrorC", {"center": v(-5.8, -17.36) * mm, "radius": 0.25 * mm});
            skCircle(sketch, "E907.MirrorC", {"center": v(-11.34, -5.5) * mm, "radius": 0.25 * mm});
            skCircle(sketch, "E908.MirrorC", {"center": v(-6.58, -12.37) * mm, "radius": 0.25 * mm});
            skCircle(sketch, "E909.MirrorC", {"center": v(-12.06, -6.53) * mm, "radius": 0.25 * mm});
            skCircle(sketch, "E910.MirrorC", {"center": v(-1.1, -19.39) * mm, "radius": 0.25 * mm});
            skCircle(sketch, "E911.MirrorC", {"center": v(-8.07, -6.55) * mm, "radius": 0.25 * mm});
            skCircle(sketch, "E912.MirrorC", {"center": v(-11.3, -1.56) * mm, "radius": 0.25 * mm});
            skCircle(sketch, "E913.MirrorC", {"center": v(-14.52, -7.47) * mm, "radius": 0.25 * mm});
            skCircle(sketch, "E914.MirrorC", {"center": v(-8.89, -22.3) * mm, "radius": 0.25 * mm});
            skCircle(sketch, "E915.MirrorC", {"center": v(-9.69, -5.5) * mm, "radius": 0.25 * mm});
            skCircle(sketch, "E916.MirrorC", {"center": v(-14.6, -16.32) * mm, "radius": 0.25 * mm});
            skCircle(sketch, "E917.MirrorC", {"center": v(-6.58, -17.31) * mm, "radius": 0.25 * mm});
            skCircle(sketch, "E918.MirrorC", {"center": v(-8.86, -19.34) * mm, "radius": 0.25 * mm});
            skCircle(sketch, "E919.MirrorC", {"center": v(-10.6, -15.3) * mm, "radius": 0.25 * mm});
            skCircle(sketch, "E920.MirrorC", {"center": v(-8.07, -3.61) * mm, "radius": 0.25 * mm});
            skCircle(sketch, "E921.MirrorC", {"center": v(-11.3, -3.56) * mm, "radius": 0.25 * mm});
            skCircle(sketch, "E922.MirrorC", {"center": v(-9.64, -2.54) * mm, "radius": 0.25 * mm});
            skCircle(sketch, "E923.MirrorC", {"center": v(-1.14, -0.67) * mm, "radius": 0.25 * mm});
            skCircle(sketch, "E924.MirrorC", {"center": v(-10.52, -5.48) * mm, "radius": 0.25 * mm});
            skCircle(sketch, "E925.MirrorC", {"center": v(-12.82, -7.45) * mm, "radius": 0.25 * mm});
            skCircle(sketch, "E926.MirrorC", {"center": v(-2.58, -5.6) * mm, "radius": 0.25 * mm});
            skCircle(sketch, "E927.MirrorC", {"center": v(-9.69, -0.57) * mm, "radius": 0.25 * mm});
            skCircle(sketch, "E928.MirrorC", {"center": v(-0.44, -7.56) * mm, "radius": 0.25 * mm});
            skCircle(sketch, "E929.MirrorC", {"center": v(-13.71, -6.47) * mm, "radius": 0.25 * mm});
            skCircle(sketch, "E930.MirrorC", {"center": v(-12.13, -11.4) * mm, "radius": 0.25 * mm});
            skCircle(sketch, "E931.MirrorC", {"center": v(-2.58, -0.67) * mm, "radius": 0.25 * mm});
            skCircle(sketch, "E932.MirrorC", {"center": v(-1.86, -14.43) * mm, "radius": 0.25 * mm});
            skCircle(sketch, "E933.MirrorC", {"center": v(-4.95, -13.47) * mm, "radius": 0.25 * mm});
            skCircle(sketch, "E934.MirrorC", {"center": v(-11.37, -24.95) * mm, "radius": 0.25 * mm});
            skCircle(sketch, "E935.MirrorC", {"center": v(-12.13, -20.3) * mm, "radius": 0.25 * mm});
            skCircle(sketch, "E936.MirrorC", {"center": v(-12.85, -21.24) * mm, "radius": 0.25 * mm});
            skCircle(sketch, "E937.MirrorC", {"center": v(-8.86, -2.59) * mm, "radius": 0.25 * mm});
            skCircle(sketch, "E938.MirrorC", {"center": v(-9.64, -7.47) * mm, "radius": 0.25 * mm});
            skCircle(sketch, "E939.MirrorC", {"center": v(-0.44, -14.44) * mm, "radius": 0.25 * mm});
            skCircle(sketch, "E940.MirrorC", {"center": v(-0.44, -2.63) * mm, "radius": 0.25 * mm});
            skCircle(sketch, "E941.MirrorC", {"center": v(-8.07, -8.55) * mm, "radius": 0.25 * mm});
            skCircle(sketch, "E942.MirrorC", {"center": v(-14.45, -9.47) * mm, "radius": 0.25 * mm});
            skCircle(sketch, "E943.MirrorC", {"center": v(-6.55, -0.6) * mm, "radius": 0.25 * mm});
            skCircle(sketch, "E944.MirrorC", {"center": v(-13.71, -1.54) * mm, "radius": 0.25 * mm});
            skCircle(sketch, "E945.MirrorC", {"center": v(-5.76, -5.58) * mm, "radius": 0.25 * mm});
            skCircle(sketch, "E946.MirrorC", {"center": v(-12.9, -12.33) * mm, "radius": 0.25 * mm});
            skCircle(sketch, "E947.MirrorC", {"center": v(-5.72, -3.63) * mm, "radius": 0.25 * mm});
            skCircle(sketch, "E948.MirrorC", {"center": v(-14.6, -11.38) * mm, "radius": 0.25 * mm});
            skCircle(sketch, "E949.MirrorC", {"center": v(-9.67, -21.27) * mm, "radius": 0.25 * mm});
            skCircle(sketch, "E950.MirrorC", {"center": v(-10.48, -14.32) * mm, "radius": 0.25 * mm});
            skCircle(sketch, "E951.MirrorC", {"center": v(-4.06, -1.64) * mm, "radius": 0.25 * mm});
            skCircle(sketch, "E952.MirrorC", {"center": v(-3.3, -2.58) * mm, "radius": 0.25 * mm});
            skCircle(sketch, "E953.MirrorC", {"center": v(-1.93, -11.46) * mm, "radius": 0.25 * mm});
            skCircle(sketch, "E954.MirrorC", {"center": v(-8.11, -0.62) * mm, "radius": 0.25 * mm});
            skCircle(sketch, "E955.MirrorC", {"center": v(-3.33, -21.31) * mm, "radius": 0.25 * mm});
            skPoint(sketch, "E956.0", {"position": v(-1.46, -24.04) * mm});
            skSolve(sketch);
        }
        {
            var Q0;
            Q0=qSketchRegion(id+"F6",true);
            extrude(context, id + "F7", {"entities" : qUnion([Q0]), "operationType" : NewBodyOperationType.ADD, "oppositeDirection" : true, "depth" : 40 * mm});
        }
    });
